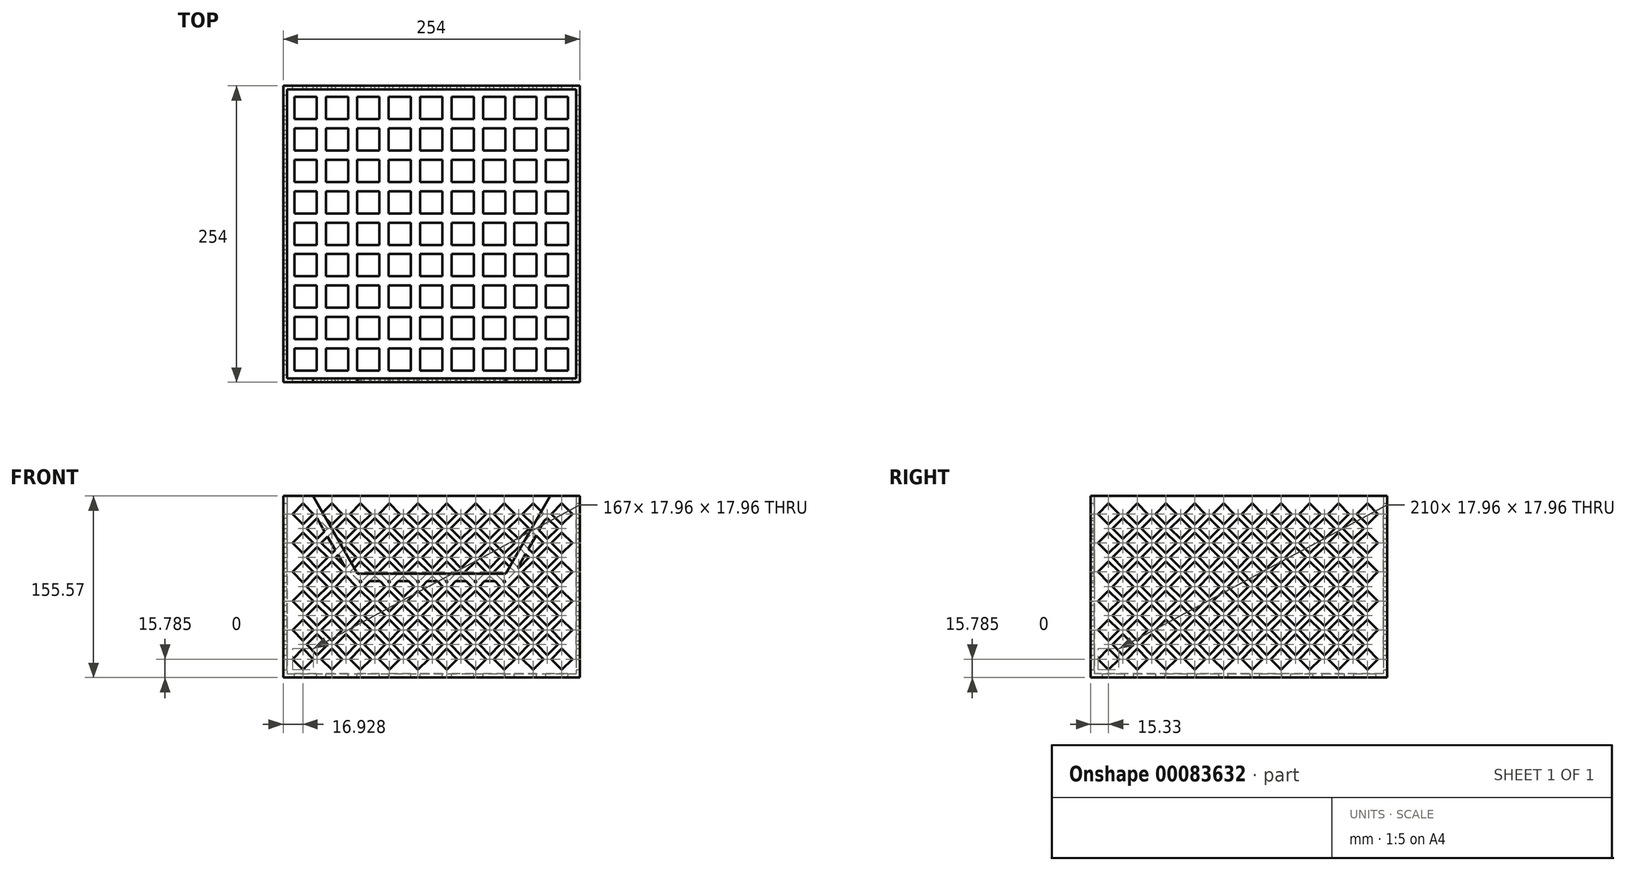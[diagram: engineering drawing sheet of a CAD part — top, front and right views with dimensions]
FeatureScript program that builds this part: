
annotation { "Feature Type Name" : "Feature", "Feature Type Description" : "" }
export const myFeature = defineFeature(function(context is Context, id is Id, definition is map)
    precondition{}
    {
        {
            var Q0;
            Q0=qCreatedBy(makeId("Top.planeOp"),FACE);
            var sketch = newSketch(context, id + "F0", { "sketchPlane" : qUnion([Q0])});
            skLineSegment(sketch, "E0.bottom", {"start": v(-127, 127) * mm, "end": v(127, 127) * mm});
            skLineSegment(sketch, "E0.top", {"start": v(-127, -127) * mm, "end": v(127, -127) * mm});
            skLineSegment(sketch, "E0.left", {"start": v(-127, 127) * mm, "end": v(-127, -127) * mm});
            skLineSegment(sketch, "E0.right", {"start": v(127, 127) * mm, "end": v(127, -127) * mm});
            skPoint(sketch, "E0.middle", {"position": v(0, 0) * mm});
            skSolve(sketch);
        }
        {
            var Q0;
            Q0 = qSketchRegion(id + "F0", true);
            extrude(context, id + "F1", {"entities" : qUnion([Q0]), "depth" : 3.17 * mm});
        }
        {
            var Q0;
            Q0=makeQuery(id+"F1.opExtrude","CAP_FACE",FACE,{"disambiguationData":[OSD([sQuery(id+"F0.wireOp",EDGE,"E0.bottom"),sQuery(id+"F0.wireOp",EDGE,"E0.top"),sQuery(id+"F0.wireOp",EDGE,"E0.left"),sQuery(id+"F0.wireOp",EDGE,"E0.right")])],"isStart":false});
            var sketch = newSketch(context, id + "F2", { "sketchPlane" : qUnion([Q0])});
            skLineSegment(sketch, "E1.bottom", {"start": v(-127, 127) * mm, "end": v(127, 127) * mm});
            skLineSegment(sketch, "E1.top", {"start": v(-127, -127) * mm, "end": v(127, -127) * mm});
            skLineSegment(sketch, "E1.left", {"start": v(-127, 127) * mm, "end": v(-127, -127) * mm});
            skLineSegment(sketch, "E1.right", {"start": v(127, 127) * mm, "end": v(127, -127) * mm});
            skPoint(sketch, "E1.middle", {"position": v(0, 0) * mm});
            skLineSegment(sketch, "E2.bottom", {"start": v(-123.82, 123.82) * mm, "end": v(123.82, 123.82) * mm});
            skLineSegment(sketch, "E2.top", {"start": v(-123.82, -123.82) * mm, "end": v(123.82, -123.82) * mm});
            skLineSegment(sketch, "E2.left", {"start": v(-123.82, 123.82) * mm, "end": v(-123.82, -123.82) * mm});
            skLineSegment(sketch, "E2.right", {"start": v(123.82, 123.82) * mm, "end": v(123.82, -123.82) * mm});
            skSolve(sketch);
        }
        {
            var Q0;
            Q0 = qSketchRegion(id + "F2", true);
            extrude(context, id + "F3", {"entities" : qUnion([Q0]), "operationType" : NewBodyOperationType.ADD, "depth" : 152.4 * mm});
        }
        {
            var Q0;
            Q0=makeQuery(id+"F3.boolean.opBoolean","MERGE",FACE,{"derivedFrom":[makeQuery(id+"F1.opExtrude","SWEPT_FACE",FACE,{"disambiguationData":[OSD([sQuery(id+"F0.wireOp",EDGE,"E0.top")])]}),makeQuery(id+"F3.opExtrude","SWEPT_FACE",FACE,{"disambiguationData":[OSD([sQuery(id+"F2.wireOp",EDGE,"E1.top")])]})]});
            var sketch = newSketch(context, id + "F4", { "sketchPlane" : qUnion([Q0])});
            skLineSegment(sketch, "E3", {"start": v(0, 155.58) * mm, "end": v(0, 88.9) * mm, "construction": true});
            skLineSegment(sketch, "E4", {"start": v(0, 88.9) * mm, "end": v(-63.5, 88.9) * mm});
            skLineSegment(sketch, "E5", {"start": v(-63.5, 88.9) * mm, "end": v(-101.6, 155.58) * mm});
            skLineSegment(sketch, "E6", {"start": v(-101.6, 155.58) * mm, "end": v(0, 155.58) * mm});
            skLineSegment(sketch, "E7.MirrorCS", {"start": v(0, 88.9) * mm, "end": v(63.5, 88.9) * mm});
            skLineSegment(sketch, "E8.MirrorCS", {"start": v(101.6, 155.58) * mm, "end": v(0, 155.58) * mm});
            skLineSegment(sketch, "E9.MirrorCS", {"start": v(63.5, 88.9) * mm, "end": v(101.6, 155.58) * mm});
            skSolve(sketch);
        }
        {
            var Q0;
            Q0 = qSketchRegion(id + "F4", true);
            extrude(context, id + "F5", {"entities" : qUnion([Q0]), "operationType" : NewBodyOperationType.REMOVE, "endBound" : BoundingType.UP_TO_NEXT, "oppositeDirection" : true, "depth" : 25.4 * mm});
        }
        {
            var Q0;
            Q0=makeQuery(id+"F3.boolean.opBoolean","MERGE",FACE,{"derivedFrom":[makeQuery(id+"F1.opExtrude","SWEPT_FACE",FACE,{"disambiguationData":[OSD([sQuery(id+"F0.wireOp",EDGE,"E0.right")])]}),makeQuery(id+"F3.opExtrude","SWEPT_FACE",FACE,{"disambiguationData":[OSD([sQuery(id+"F2.wireOp",EDGE,"E1.right")])]})]});
            var sketch = newSketch(context, id + "F6", { "sketchPlane" : qUnion([Q0])});
            skLineSegment(sketch, "E10", {"start": v(-111.67, 149.23) * mm, "end": v(-120.65, 140.24) * mm});
            skLineSegment(sketch, "E11", {"start": v(-120.65, 140.24) * mm, "end": v(-111.67, 131.26) * mm});
            skLineSegment(sketch, "E12", {"start": v(-111.67, 131.26) * mm, "end": v(-102.69, 140.24) * mm});
            skLineSegment(sketch, "E13", {"start": v(-102.69, 140.24) * mm, "end": v(-111.67, 149.23) * mm});
            skLineSegment(sketch, "E14", {"start": v(-111.67, 131.26) * mm, "end": v(-88.6, 131.26) * mm, "construction": true});
            skLineSegment(sketch, "E15.0.1.0", {"start": v(-120.65, 115.35) * mm, "end": v(-111.67, 106.37) * mm});
            skLineSegment(sketch, "E15.0.1.1", {"start": v(-111.67, 106.37) * mm, "end": v(-102.69, 115.35) * mm});
            skLineSegment(sketch, "E15.0.1.2", {"start": v(-102.69, 115.35) * mm, "end": v(-111.67, 124.33) * mm});
            skLineSegment(sketch, "E15.0.1.3", {"start": v(-111.67, 124.33) * mm, "end": v(-120.65, 115.35) * mm});
            skLineSegment(sketch, "E15.0.2.0", {"start": v(-120.65, 90.46) * mm, "end": v(-111.67, 81.48) * mm});
            skLineSegment(sketch, "E15.0.2.1", {"start": v(-111.67, 81.48) * mm, "end": v(-102.69, 90.46) * mm});
            skLineSegment(sketch, "E15.0.2.2", {"start": v(-102.69, 90.46) * mm, "end": v(-111.67, 99.44) * mm});
            skLineSegment(sketch, "E15.0.2.3", {"start": v(-111.67, 99.44) * mm, "end": v(-120.65, 90.46) * mm});
            skLineSegment(sketch, "E15.0.3.0", {"start": v(-120.65, 65.57) * mm, "end": v(-111.67, 56.59) * mm});
            skLineSegment(sketch, "E15.0.3.1", {"start": v(-111.67, 56.59) * mm, "end": v(-102.69, 65.57) * mm});
            skLineSegment(sketch, "E15.0.3.2", {"start": v(-102.69, 65.57) * mm, "end": v(-111.67, 74.55) * mm});
            skLineSegment(sketch, "E15.0.3.3", {"start": v(-111.67, 74.55) * mm, "end": v(-120.65, 65.57) * mm});
            skLineSegment(sketch, "E15.0.4.0", {"start": v(-120.65, 40.68) * mm, "end": v(-111.67, 31.7) * mm});
            skLineSegment(sketch, "E15.0.4.1", {"start": v(-111.67, 31.7) * mm, "end": v(-102.69, 40.68) * mm});
            skLineSegment(sketch, "E15.0.4.2", {"start": v(-102.69, 40.68) * mm, "end": v(-111.67, 49.66) * mm});
            skLineSegment(sketch, "E15.0.4.3", {"start": v(-111.67, 49.66) * mm, "end": v(-120.65, 40.68) * mm});
            skLineSegment(sketch, "E15.0.5.0", {"start": v(-120.65, 15.78) * mm, "end": v(-111.67, 6.8) * mm});
            skLineSegment(sketch, "E15.0.5.1", {"start": v(-111.67, 6.8) * mm, "end": v(-102.69, 15.78) * mm});
            skLineSegment(sketch, "E15.0.5.2", {"start": v(-102.69, 15.78) * mm, "end": v(-111.67, 24.77) * mm});
            skLineSegment(sketch, "E15.0.5.3", {"start": v(-111.67, 24.77) * mm, "end": v(-120.65, 15.78) * mm});
            skLineSegment(sketch, "E15.1.0.0", {"start": v(-96.01, 140.24) * mm, "end": v(-87.03, 131.26) * mm});
            skLineSegment(sketch, "E15.1.0.1", {"start": v(-87.03, 131.26) * mm, "end": v(-78.05, 140.24) * mm});
            skLineSegment(sketch, "E15.1.0.2", {"start": v(-78.05, 140.24) * mm, "end": v(-87.03, 149.23) * mm});
            skLineSegment(sketch, "E15.1.0.3", {"start": v(-87.03, 149.23) * mm, "end": v(-96.01, 140.24) * mm});
            skLineSegment(sketch, "E15.1.1.0", {"start": v(-96.01, 115.35) * mm, "end": v(-87.03, 106.37) * mm});
            skLineSegment(sketch, "E15.1.1.1", {"start": v(-87.03, 106.37) * mm, "end": v(-78.05, 115.35) * mm});
            skLineSegment(sketch, "E15.1.1.2", {"start": v(-78.05, 115.35) * mm, "end": v(-87.03, 124.33) * mm});
            skLineSegment(sketch, "E15.1.1.3", {"start": v(-87.03, 124.33) * mm, "end": v(-96.01, 115.35) * mm});
            skLineSegment(sketch, "E15.1.2.0", {"start": v(-96.01, 90.46) * mm, "end": v(-87.03, 81.48) * mm});
            skLineSegment(sketch, "E15.1.2.1", {"start": v(-87.03, 81.48) * mm, "end": v(-78.05, 90.46) * mm});
            skLineSegment(sketch, "E15.1.2.2", {"start": v(-78.05, 90.46) * mm, "end": v(-87.03, 99.44) * mm});
            skLineSegment(sketch, "E15.1.2.3", {"start": v(-87.03, 99.44) * mm, "end": v(-96.01, 90.46) * mm});
            skLineSegment(sketch, "E15.1.3.0", {"start": v(-96.01, 65.57) * mm, "end": v(-87.03, 56.59) * mm});
            skLineSegment(sketch, "E15.1.3.1", {"start": v(-87.03, 56.59) * mm, "end": v(-78.05, 65.57) * mm});
            skLineSegment(sketch, "E15.1.3.2", {"start": v(-78.05, 65.57) * mm, "end": v(-87.03, 74.55) * mm});
            skLineSegment(sketch, "E15.1.3.3", {"start": v(-87.03, 74.55) * mm, "end": v(-96.01, 65.57) * mm});
            skLineSegment(sketch, "E15.1.4.0", {"start": v(-96.01, 40.68) * mm, "end": v(-87.03, 31.7) * mm});
            skLineSegment(sketch, "E15.1.4.1", {"start": v(-87.03, 31.7) * mm, "end": v(-78.05, 40.68) * mm});
            skLineSegment(sketch, "E15.1.4.2", {"start": v(-78.05, 40.68) * mm, "end": v(-87.03, 49.66) * mm});
            skLineSegment(sketch, "E15.1.4.3", {"start": v(-87.03, 49.66) * mm, "end": v(-96.01, 40.68) * mm});
            skLineSegment(sketch, "E15.1.5.0", {"start": v(-96.01, 15.78) * mm, "end": v(-87.03, 6.8) * mm});
            skLineSegment(sketch, "E15.1.5.1", {"start": v(-87.03, 6.8) * mm, "end": v(-78.05, 15.78) * mm});
            skLineSegment(sketch, "E15.1.5.2", {"start": v(-78.05, 15.78) * mm, "end": v(-87.03, 24.77) * mm});
            skLineSegment(sketch, "E15.1.5.3", {"start": v(-87.03, 24.77) * mm, "end": v(-96.01, 15.78) * mm});
            skLineSegment(sketch, "E15.2.0.0", {"start": v(-71.37, 140.24) * mm, "end": v(-62.4, 131.26) * mm});
            skLineSegment(sketch, "E15.2.0.1", {"start": v(-62.4, 131.26) * mm, "end": v(-53.41, 140.24) * mm});
            skLineSegment(sketch, "E15.2.0.2", {"start": v(-53.41, 140.24) * mm, "end": v(-62.4, 149.23) * mm});
            skLineSegment(sketch, "E15.2.0.3", {"start": v(-62.4, 149.23) * mm, "end": v(-71.37, 140.24) * mm});
            skLineSegment(sketch, "E15.2.1.0", {"start": v(-71.37, 115.35) * mm, "end": v(-62.4, 106.37) * mm});
            skLineSegment(sketch, "E15.2.1.1", {"start": v(-62.4, 106.37) * mm, "end": v(-53.41, 115.35) * mm});
            skLineSegment(sketch, "E15.2.1.2", {"start": v(-53.41, 115.35) * mm, "end": v(-62.4, 124.33) * mm});
            skLineSegment(sketch, "E15.2.1.3", {"start": v(-62.4, 124.33) * mm, "end": v(-71.37, 115.35) * mm});
            skLineSegment(sketch, "E15.2.2.0", {"start": v(-71.37, 90.46) * mm, "end": v(-62.4, 81.48) * mm});
            skLineSegment(sketch, "E15.2.2.1", {"start": v(-62.4, 81.48) * mm, "end": v(-53.41, 90.46) * mm});
            skLineSegment(sketch, "E15.2.2.2", {"start": v(-53.41, 90.46) * mm, "end": v(-62.4, 99.44) * mm});
            skLineSegment(sketch, "E15.2.2.3", {"start": v(-62.4, 99.44) * mm, "end": v(-71.37, 90.46) * mm});
            skLineSegment(sketch, "E15.2.3.0", {"start": v(-71.37, 65.57) * mm, "end": v(-62.4, 56.59) * mm});
            skLineSegment(sketch, "E15.2.3.1", {"start": v(-62.4, 56.59) * mm, "end": v(-53.41, 65.57) * mm});
            skLineSegment(sketch, "E15.2.3.2", {"start": v(-53.41, 65.57) * mm, "end": v(-62.4, 74.55) * mm});
            skLineSegment(sketch, "E15.2.3.3", {"start": v(-62.4, 74.55) * mm, "end": v(-71.37, 65.57) * mm});
            skLineSegment(sketch, "E15.2.4.0", {"start": v(-71.37, 40.68) * mm, "end": v(-62.4, 31.7) * mm});
            skLineSegment(sketch, "E15.2.4.1", {"start": v(-62.4, 31.7) * mm, "end": v(-53.41, 40.68) * mm});
            skLineSegment(sketch, "E15.2.4.2", {"start": v(-53.41, 40.68) * mm, "end": v(-62.4, 49.66) * mm});
            skLineSegment(sketch, "E15.2.4.3", {"start": v(-62.4, 49.66) * mm, "end": v(-71.37, 40.68) * mm});
            skLineSegment(sketch, "E15.2.5.0", {"start": v(-71.37, 15.78) * mm, "end": v(-62.4, 6.8) * mm});
            skLineSegment(sketch, "E15.2.5.1", {"start": v(-62.4, 6.8) * mm, "end": v(-53.41, 15.78) * mm});
            skLineSegment(sketch, "E15.2.5.2", {"start": v(-53.41, 15.78) * mm, "end": v(-62.4, 24.77) * mm});
            skLineSegment(sketch, "E15.2.5.3", {"start": v(-62.4, 24.77) * mm, "end": v(-71.37, 15.78) * mm});
            skLineSegment(sketch, "E15.3.0.0", {"start": v(-46.74, 140.24) * mm, "end": v(-37.76, 131.26) * mm});
            skLineSegment(sketch, "E15.3.0.1", {"start": v(-37.76, 131.26) * mm, "end": v(-28.78, 140.24) * mm});
            skLineSegment(sketch, "E15.3.0.2", {"start": v(-28.78, 140.24) * mm, "end": v(-37.76, 149.23) * mm});
            skLineSegment(sketch, "E15.3.0.3", {"start": v(-37.76, 149.23) * mm, "end": v(-46.74, 140.24) * mm});
            skLineSegment(sketch, "E15.3.1.0", {"start": v(-46.74, 115.35) * mm, "end": v(-37.76, 106.37) * mm});
            skLineSegment(sketch, "E15.3.1.1", {"start": v(-37.76, 106.37) * mm, "end": v(-28.78, 115.35) * mm});
            skLineSegment(sketch, "E15.3.1.2", {"start": v(-28.78, 115.35) * mm, "end": v(-37.76, 124.33) * mm});
            skLineSegment(sketch, "E15.3.1.3", {"start": v(-37.76, 124.33) * mm, "end": v(-46.74, 115.35) * mm});
            skLineSegment(sketch, "E15.3.2.0", {"start": v(-46.74, 90.46) * mm, "end": v(-37.76, 81.48) * mm});
            skLineSegment(sketch, "E15.3.2.1", {"start": v(-37.76, 81.48) * mm, "end": v(-28.78, 90.46) * mm});
            skLineSegment(sketch, "E15.3.2.2", {"start": v(-28.78, 90.46) * mm, "end": v(-37.76, 99.44) * mm});
            skLineSegment(sketch, "E15.3.2.3", {"start": v(-37.76, 99.44) * mm, "end": v(-46.74, 90.46) * mm});
            skLineSegment(sketch, "E15.3.3.0", {"start": v(-46.74, 65.57) * mm, "end": v(-37.76, 56.59) * mm});
            skLineSegment(sketch, "E15.3.3.1", {"start": v(-37.76, 56.59) * mm, "end": v(-28.78, 65.57) * mm});
            skLineSegment(sketch, "E15.3.3.2", {"start": v(-28.78, 65.57) * mm, "end": v(-37.76, 74.55) * mm});
            skLineSegment(sketch, "E15.3.3.3", {"start": v(-37.76, 74.55) * mm, "end": v(-46.74, 65.57) * mm});
            skLineSegment(sketch, "E15.3.4.0", {"start": v(-46.74, 40.68) * mm, "end": v(-37.76, 31.7) * mm});
            skLineSegment(sketch, "E15.3.4.1", {"start": v(-37.76, 31.7) * mm, "end": v(-28.78, 40.68) * mm});
            skLineSegment(sketch, "E15.3.4.2", {"start": v(-28.78, 40.68) * mm, "end": v(-37.76, 49.66) * mm});
            skLineSegment(sketch, "E15.3.4.3", {"start": v(-37.76, 49.66) * mm, "end": v(-46.74, 40.68) * mm});
            skLineSegment(sketch, "E15.3.5.0", {"start": v(-46.74, 15.78) * mm, "end": v(-37.76, 6.8) * mm});
            skLineSegment(sketch, "E15.3.5.1", {"start": v(-37.76, 6.8) * mm, "end": v(-28.78, 15.78) * mm});
            skLineSegment(sketch, "E15.3.5.2", {"start": v(-28.78, 15.78) * mm, "end": v(-37.76, 24.77) * mm});
            skLineSegment(sketch, "E15.3.5.3", {"start": v(-37.76, 24.77) * mm, "end": v(-46.74, 15.78) * mm});
            skLineSegment(sketch, "E15.4.0.0", {"start": v(-22.1, 140.24) * mm, "end": v(-13.12, 131.26) * mm});
            skLineSegment(sketch, "E15.4.0.1", {"start": v(-13.12, 131.26) * mm, "end": v(-4.14, 140.24) * mm});
            skLineSegment(sketch, "E15.4.0.2", {"start": v(-4.14, 140.24) * mm, "end": v(-13.12, 149.23) * mm});
            skLineSegment(sketch, "E15.4.0.3", {"start": v(-13.12, 149.23) * mm, "end": v(-22.1, 140.24) * mm});
            skLineSegment(sketch, "E15.4.1.0", {"start": v(-22.1, 115.35) * mm, "end": v(-13.12, 106.37) * mm});
            skLineSegment(sketch, "E15.4.1.1", {"start": v(-13.12, 106.37) * mm, "end": v(-4.14, 115.35) * mm});
            skLineSegment(sketch, "E15.4.1.2", {"start": v(-4.14, 115.35) * mm, "end": v(-13.12, 124.33) * mm});
            skLineSegment(sketch, "E15.4.1.3", {"start": v(-13.12, 124.33) * mm, "end": v(-22.1, 115.35) * mm});
            skLineSegment(sketch, "E15.4.2.0", {"start": v(-22.1, 90.46) * mm, "end": v(-13.12, 81.48) * mm});
            skLineSegment(sketch, "E15.4.2.1", {"start": v(-13.12, 81.48) * mm, "end": v(-4.14, 90.46) * mm});
            skLineSegment(sketch, "E15.4.2.2", {"start": v(-4.14, 90.46) * mm, "end": v(-13.12, 99.44) * mm});
            skLineSegment(sketch, "E15.4.2.3", {"start": v(-13.12, 99.44) * mm, "end": v(-22.1, 90.46) * mm});
            skLineSegment(sketch, "E15.4.3.0", {"start": v(-22.1, 65.57) * mm, "end": v(-13.12, 56.59) * mm});
            skLineSegment(sketch, "E15.4.3.1", {"start": v(-13.12, 56.59) * mm, "end": v(-4.14, 65.57) * mm});
            skLineSegment(sketch, "E15.4.3.2", {"start": v(-4.14, 65.57) * mm, "end": v(-13.12, 74.55) * mm});
            skLineSegment(sketch, "E15.4.3.3", {"start": v(-13.12, 74.55) * mm, "end": v(-22.1, 65.57) * mm});
            skLineSegment(sketch, "E15.4.4.0", {"start": v(-22.1, 40.68) * mm, "end": v(-13.12, 31.7) * mm});
            skLineSegment(sketch, "E15.4.4.1", {"start": v(-13.12, 31.7) * mm, "end": v(-4.14, 40.68) * mm});
            skLineSegment(sketch, "E15.4.4.2", {"start": v(-4.14, 40.68) * mm, "end": v(-13.12, 49.66) * mm});
            skLineSegment(sketch, "E15.4.4.3", {"start": v(-13.12, 49.66) * mm, "end": v(-22.1, 40.68) * mm});
            skLineSegment(sketch, "E15.4.5.0", {"start": v(-22.1, 15.78) * mm, "end": v(-13.12, 6.8) * mm});
            skLineSegment(sketch, "E15.4.5.1", {"start": v(-13.12, 6.8) * mm, "end": v(-4.14, 15.78) * mm});
            skLineSegment(sketch, "E15.4.5.2", {"start": v(-4.14, 15.78) * mm, "end": v(-13.12, 24.77) * mm});
            skLineSegment(sketch, "E15.4.5.3", {"start": v(-13.12, 24.77) * mm, "end": v(-22.1, 15.78) * mm});
            skLineSegment(sketch, "E15.5.0.0", {"start": v(2.54, 140.24) * mm, "end": v(11.52, 131.26) * mm});
            skLineSegment(sketch, "E15.5.0.1", {"start": v(11.52, 131.26) * mm, "end": v(20.5, 140.24) * mm});
            skLineSegment(sketch, "E15.5.0.2", {"start": v(20.5, 140.24) * mm, "end": v(11.52, 149.23) * mm});
            skLineSegment(sketch, "E15.5.0.3", {"start": v(11.52, 149.23) * mm, "end": v(2.54, 140.24) * mm});
            skLineSegment(sketch, "E15.5.1.0", {"start": v(2.54, 115.35) * mm, "end": v(11.52, 106.37) * mm});
            skLineSegment(sketch, "E15.5.1.1", {"start": v(11.52, 106.37) * mm, "end": v(20.5, 115.35) * mm});
            skLineSegment(sketch, "E15.5.1.2", {"start": v(20.5, 115.35) * mm, "end": v(11.52, 124.33) * mm});
            skLineSegment(sketch, "E15.5.1.3", {"start": v(11.52, 124.33) * mm, "end": v(2.54, 115.35) * mm});
            skLineSegment(sketch, "E15.5.2.0", {"start": v(2.54, 90.46) * mm, "end": v(11.52, 81.48) * mm});
            skLineSegment(sketch, "E15.5.2.1", {"start": v(11.52, 81.48) * mm, "end": v(20.5, 90.46) * mm});
            skLineSegment(sketch, "E15.5.2.2", {"start": v(20.5, 90.46) * mm, "end": v(11.52, 99.44) * mm});
            skLineSegment(sketch, "E15.5.2.3", {"start": v(11.52, 99.44) * mm, "end": v(2.54, 90.46) * mm});
            skLineSegment(sketch, "E15.5.3.0", {"start": v(2.54, 65.57) * mm, "end": v(11.52, 56.59) * mm});
            skLineSegment(sketch, "E15.5.3.1", {"start": v(11.52, 56.59) * mm, "end": v(20.5, 65.57) * mm});
            skLineSegment(sketch, "E15.5.3.2", {"start": v(20.5, 65.57) * mm, "end": v(11.52, 74.55) * mm});
            skLineSegment(sketch, "E15.5.3.3", {"start": v(11.52, 74.55) * mm, "end": v(2.54, 65.57) * mm});
            skLineSegment(sketch, "E15.5.4.0", {"start": v(2.54, 40.68) * mm, "end": v(11.52, 31.7) * mm});
            skLineSegment(sketch, "E15.5.4.1", {"start": v(11.52, 31.7) * mm, "end": v(20.5, 40.68) * mm});
            skLineSegment(sketch, "E15.5.4.2", {"start": v(20.5, 40.68) * mm, "end": v(11.52, 49.66) * mm});
            skLineSegment(sketch, "E15.5.4.3", {"start": v(11.52, 49.66) * mm, "end": v(2.54, 40.68) * mm});
            skLineSegment(sketch, "E15.5.5.0", {"start": v(2.54, 15.78) * mm, "end": v(11.52, 6.8) * mm});
            skLineSegment(sketch, "E15.5.5.1", {"start": v(11.52, 6.8) * mm, "end": v(20.5, 15.78) * mm});
            skLineSegment(sketch, "E15.5.5.2", {"start": v(20.5, 15.78) * mm, "end": v(11.52, 24.77) * mm});
            skLineSegment(sketch, "E15.5.5.3", {"start": v(11.52, 24.77) * mm, "end": v(2.54, 15.78) * mm});
            skLineSegment(sketch, "E15.6.0.0", {"start": v(27.18, 140.24) * mm, "end": v(36.16, 131.26) * mm});
            skLineSegment(sketch, "E15.6.0.1", {"start": v(36.16, 131.26) * mm, "end": v(45.14, 140.24) * mm});
            skLineSegment(sketch, "E15.6.0.2", {"start": v(45.14, 140.24) * mm, "end": v(36.16, 149.23) * mm});
            skLineSegment(sketch, "E15.6.0.3", {"start": v(36.16, 149.23) * mm, "end": v(27.18, 140.24) * mm});
            skLineSegment(sketch, "E15.6.1.0", {"start": v(27.18, 115.35) * mm, "end": v(36.16, 106.37) * mm});
            skLineSegment(sketch, "E15.6.1.1", {"start": v(36.16, 106.37) * mm, "end": v(45.14, 115.35) * mm});
            skLineSegment(sketch, "E15.6.1.2", {"start": v(45.14, 115.35) * mm, "end": v(36.16, 124.33) * mm});
            skLineSegment(sketch, "E15.6.1.3", {"start": v(36.16, 124.33) * mm, "end": v(27.18, 115.35) * mm});
            skLineSegment(sketch, "E15.6.2.0", {"start": v(27.18, 90.46) * mm, "end": v(36.16, 81.48) * mm});
            skLineSegment(sketch, "E15.6.2.1", {"start": v(36.16, 81.48) * mm, "end": v(45.14, 90.46) * mm});
            skLineSegment(sketch, "E15.6.2.2", {"start": v(45.14, 90.46) * mm, "end": v(36.16, 99.44) * mm});
            skLineSegment(sketch, "E15.6.2.3", {"start": v(36.16, 99.44) * mm, "end": v(27.18, 90.46) * mm});
            skLineSegment(sketch, "E15.6.3.0", {"start": v(27.18, 65.57) * mm, "end": v(36.16, 56.59) * mm});
            skLineSegment(sketch, "E15.6.3.1", {"start": v(36.16, 56.59) * mm, "end": v(45.14, 65.57) * mm});
            skLineSegment(sketch, "E15.6.3.2", {"start": v(45.14, 65.57) * mm, "end": v(36.16, 74.55) * mm});
            skLineSegment(sketch, "E15.6.3.3", {"start": v(36.16, 74.55) * mm, "end": v(27.18, 65.57) * mm});
            skLineSegment(sketch, "E15.6.4.0", {"start": v(27.18, 40.68) * mm, "end": v(36.16, 31.7) * mm});
            skLineSegment(sketch, "E15.6.4.1", {"start": v(36.16, 31.7) * mm, "end": v(45.14, 40.68) * mm});
            skLineSegment(sketch, "E15.6.4.2", {"start": v(45.14, 40.68) * mm, "end": v(36.16, 49.66) * mm});
            skLineSegment(sketch, "E15.6.4.3", {"start": v(36.16, 49.66) * mm, "end": v(27.18, 40.68) * mm});
            skLineSegment(sketch, "E15.6.5.0", {"start": v(27.18, 15.78) * mm, "end": v(36.16, 6.8) * mm});
            skLineSegment(sketch, "E15.6.5.1", {"start": v(36.16, 6.8) * mm, "end": v(45.14, 15.78) * mm});
            skLineSegment(sketch, "E15.6.5.2", {"start": v(45.14, 15.78) * mm, "end": v(36.16, 24.77) * mm});
            skLineSegment(sketch, "E15.6.5.3", {"start": v(36.16, 24.77) * mm, "end": v(27.18, 15.78) * mm});
            skLineSegment(sketch, "E15.7.0.0", {"start": v(51.82, 140.24) * mm, "end": v(60.8, 131.26) * mm});
            skLineSegment(sketch, "E15.7.0.1", {"start": v(60.8, 131.26) * mm, "end": v(69.78, 140.24) * mm});
            skLineSegment(sketch, "E15.7.0.2", {"start": v(69.78, 140.24) * mm, "end": v(60.8, 149.23) * mm});
            skLineSegment(sketch, "E15.7.0.3", {"start": v(60.8, 149.23) * mm, "end": v(51.82, 140.24) * mm});
            skLineSegment(sketch, "E15.7.1.0", {"start": v(51.82, 115.35) * mm, "end": v(60.8, 106.37) * mm});
            skLineSegment(sketch, "E15.7.1.1", {"start": v(60.8, 106.37) * mm, "end": v(69.78, 115.35) * mm});
            skLineSegment(sketch, "E15.7.1.2", {"start": v(69.78, 115.35) * mm, "end": v(60.8, 124.33) * mm});
            skLineSegment(sketch, "E15.7.1.3", {"start": v(60.8, 124.33) * mm, "end": v(51.82, 115.35) * mm});
            skLineSegment(sketch, "E15.7.2.0", {"start": v(51.82, 90.46) * mm, "end": v(60.8, 81.48) * mm});
            skLineSegment(sketch, "E15.7.2.1", {"start": v(60.8, 81.48) * mm, "end": v(69.78, 90.46) * mm});
            skLineSegment(sketch, "E15.7.2.2", {"start": v(69.78, 90.46) * mm, "end": v(60.8, 99.44) * mm});
            skLineSegment(sketch, "E15.7.2.3", {"start": v(60.8, 99.44) * mm, "end": v(51.82, 90.46) * mm});
            skLineSegment(sketch, "E15.7.3.0", {"start": v(51.82, 65.57) * mm, "end": v(60.8, 56.59) * mm});
            skLineSegment(sketch, "E15.7.3.1", {"start": v(60.8, 56.59) * mm, "end": v(69.78, 65.57) * mm});
            skLineSegment(sketch, "E15.7.3.2", {"start": v(69.78, 65.57) * mm, "end": v(60.8, 74.55) * mm});
            skLineSegment(sketch, "E15.7.3.3", {"start": v(60.8, 74.55) * mm, "end": v(51.82, 65.57) * mm});
            skLineSegment(sketch, "E15.7.4.0", {"start": v(51.82, 40.68) * mm, "end": v(60.8, 31.7) * mm});
            skLineSegment(sketch, "E15.7.4.1", {"start": v(60.8, 31.7) * mm, "end": v(69.78, 40.68) * mm});
            skLineSegment(sketch, "E15.7.4.2", {"start": v(69.78, 40.68) * mm, "end": v(60.8, 49.66) * mm});
            skLineSegment(sketch, "E15.7.4.3", {"start": v(60.8, 49.66) * mm, "end": v(51.82, 40.68) * mm});
            skLineSegment(sketch, "E15.7.5.0", {"start": v(51.82, 15.78) * mm, "end": v(60.8, 6.8) * mm});
            skLineSegment(sketch, "E15.7.5.1", {"start": v(60.8, 6.8) * mm, "end": v(69.78, 15.78) * mm});
            skLineSegment(sketch, "E15.7.5.2", {"start": v(69.78, 15.78) * mm, "end": v(60.8, 24.77) * mm});
            skLineSegment(sketch, "E15.7.5.3", {"start": v(60.8, 24.77) * mm, "end": v(51.82, 15.78) * mm});
            skLineSegment(sketch, "E15.8.0.0", {"start": v(76.45, 140.24) * mm, "end": v(85.43, 131.26) * mm});
            skLineSegment(sketch, "E15.8.0.1", {"start": v(85.43, 131.26) * mm, "end": v(94.41, 140.24) * mm});
            skLineSegment(sketch, "E15.8.0.2", {"start": v(94.41, 140.24) * mm, "end": v(85.43, 149.23) * mm});
            skLineSegment(sketch, "E15.8.0.3", {"start": v(85.43, 149.23) * mm, "end": v(76.45, 140.24) * mm});
            skLineSegment(sketch, "E15.8.1.0", {"start": v(76.45, 115.35) * mm, "end": v(85.43, 106.37) * mm});
            skLineSegment(sketch, "E15.8.1.1", {"start": v(85.43, 106.37) * mm, "end": v(94.41, 115.35) * mm});
            skLineSegment(sketch, "E15.8.1.2", {"start": v(94.41, 115.35) * mm, "end": v(85.43, 124.33) * mm});
            skLineSegment(sketch, "E15.8.1.3", {"start": v(85.43, 124.33) * mm, "end": v(76.45, 115.35) * mm});
            skLineSegment(sketch, "E15.8.2.0", {"start": v(76.45, 90.46) * mm, "end": v(85.43, 81.48) * mm});
            skLineSegment(sketch, "E15.8.2.1", {"start": v(85.43, 81.48) * mm, "end": v(94.41, 90.46) * mm});
            skLineSegment(sketch, "E15.8.2.2", {"start": v(94.41, 90.46) * mm, "end": v(85.43, 99.44) * mm});
            skLineSegment(sketch, "E15.8.2.3", {"start": v(85.43, 99.44) * mm, "end": v(76.45, 90.46) * mm});
            skLineSegment(sketch, "E15.8.3.0", {"start": v(76.45, 65.57) * mm, "end": v(85.43, 56.59) * mm});
            skLineSegment(sketch, "E15.8.3.1", {"start": v(85.43, 56.59) * mm, "end": v(94.41, 65.57) * mm});
            skLineSegment(sketch, "E15.8.3.2", {"start": v(94.41, 65.57) * mm, "end": v(85.43, 74.55) * mm});
            skLineSegment(sketch, "E15.8.3.3", {"start": v(85.43, 74.55) * mm, "end": v(76.45, 65.57) * mm});
            skLineSegment(sketch, "E15.8.4.0", {"start": v(76.45, 40.68) * mm, "end": v(85.43, 31.7) * mm});
            skLineSegment(sketch, "E15.8.4.1", {"start": v(85.43, 31.7) * mm, "end": v(94.41, 40.68) * mm});
            skLineSegment(sketch, "E15.8.4.2", {"start": v(94.41, 40.68) * mm, "end": v(85.43, 49.66) * mm});
            skLineSegment(sketch, "E15.8.4.3", {"start": v(85.43, 49.66) * mm, "end": v(76.45, 40.68) * mm});
            skLineSegment(sketch, "E15.8.5.0", {"start": v(76.45, 15.78) * mm, "end": v(85.43, 6.8) * mm});
            skLineSegment(sketch, "E15.8.5.1", {"start": v(85.43, 6.8) * mm, "end": v(94.41, 15.78) * mm});
            skLineSegment(sketch, "E15.8.5.2", {"start": v(94.41, 15.78) * mm, "end": v(85.43, 24.77) * mm});
            skLineSegment(sketch, "E15.8.5.3", {"start": v(85.43, 24.77) * mm, "end": v(76.45, 15.78) * mm});
            skLineSegment(sketch, "E15.9.0.0", {"start": v(101.1, 140.24) * mm, "end": v(110.07, 131.26) * mm});
            skLineSegment(sketch, "E15.9.0.1", {"start": v(110.07, 131.26) * mm, "end": v(119.05, 140.24) * mm});
            skLineSegment(sketch, "E15.9.0.2", {"start": v(119.05, 140.24) * mm, "end": v(110.07, 149.23) * mm});
            skLineSegment(sketch, "E15.9.0.3", {"start": v(110.07, 149.23) * mm, "end": v(101.1, 140.24) * mm});
            skLineSegment(sketch, "E15.9.1.0", {"start": v(101.1, 115.35) * mm, "end": v(110.07, 106.37) * mm});
            skLineSegment(sketch, "E15.9.1.1", {"start": v(110.07, 106.37) * mm, "end": v(119.05, 115.35) * mm});
            skLineSegment(sketch, "E15.9.1.2", {"start": v(119.05, 115.35) * mm, "end": v(110.07, 124.33) * mm});
            skLineSegment(sketch, "E15.9.1.3", {"start": v(110.07, 124.33) * mm, "end": v(101.1, 115.35) * mm});
            skLineSegment(sketch, "E15.9.2.0", {"start": v(101.1, 90.46) * mm, "end": v(110.07, 81.48) * mm});
            skLineSegment(sketch, "E15.9.2.1", {"start": v(110.07, 81.48) * mm, "end": v(119.05, 90.46) * mm});
            skLineSegment(sketch, "E15.9.2.2", {"start": v(119.05, 90.46) * mm, "end": v(110.07, 99.44) * mm});
            skLineSegment(sketch, "E15.9.2.3", {"start": v(110.07, 99.44) * mm, "end": v(101.1, 90.46) * mm});
            skLineSegment(sketch, "E15.9.3.0", {"start": v(101.1, 65.57) * mm, "end": v(110.07, 56.59) * mm});
            skLineSegment(sketch, "E15.9.3.1", {"start": v(110.07, 56.59) * mm, "end": v(119.05, 65.57) * mm});
            skLineSegment(sketch, "E15.9.3.2", {"start": v(119.05, 65.57) * mm, "end": v(110.07, 74.55) * mm});
            skLineSegment(sketch, "E15.9.3.3", {"start": v(110.07, 74.55) * mm, "end": v(101.1, 65.57) * mm});
            skLineSegment(sketch, "E15.9.4.0", {"start": v(101.1, 40.68) * mm, "end": v(110.07, 31.7) * mm});
            skLineSegment(sketch, "E15.9.4.1", {"start": v(110.07, 31.7) * mm, "end": v(119.05, 40.68) * mm});
            skLineSegment(sketch, "E15.9.4.2", {"start": v(119.05, 40.68) * mm, "end": v(110.07, 49.66) * mm});
            skLineSegment(sketch, "E15.9.4.3", {"start": v(110.07, 49.66) * mm, "end": v(101.1, 40.68) * mm});
            skLineSegment(sketch, "E15.9.5.0", {"start": v(101.1, 15.78) * mm, "end": v(110.07, 6.8) * mm});
            skLineSegment(sketch, "E15.9.5.1", {"start": v(110.07, 6.8) * mm, "end": v(119.05, 15.78) * mm});
            skLineSegment(sketch, "E15.9.5.2", {"start": v(119.05, 15.78) * mm, "end": v(110.07, 24.77) * mm});
            skLineSegment(sketch, "E15.9.5.3", {"start": v(110.07, 24.77) * mm, "end": v(101.1, 15.78) * mm});
            skLineSegment(sketch, "E15.direction1", {"start": v(-111.67, 131.26) * mm, "end": v(-87.03, 131.26) * mm, "construction": true});
            skLineSegment(sketch, "E15.direction2", {"start": v(-111.67, 131.26) * mm, "end": v(-111.67, 106.37) * mm, "construction": true});
            skSolve(sketch);
        }
        {
            var Q0;
            Q0 = qSketchRegion(id + "F6", true);
            extrude(context, id + "F7", {"entities" : qUnion([Q0]), "operationType" : NewBodyOperationType.REMOVE, "endBound" : BoundingType.THROUGH_ALL, "oppositeDirection" : true, "depth" : 25.4 * mm});
        }
        {
            var Q0;
            Q0=makeQuery(id+"F3.boolean.opBoolean","MERGE",FACE,{"derivedFrom":[makeQuery(id+"F1.opExtrude","SWEPT_FACE",FACE,{"disambiguationData":[OSD([sQuery(id+"F0.wireOp",EDGE,"E0.right")])]}),makeQuery(id+"F3.opExtrude","SWEPT_FACE",FACE,{"disambiguationData":[OSD([sQuery(id+"F2.wireOp",EDGE,"E1.right")])]})]});
            var sketch = newSketch(context, id + "F8", { "sketchPlane" : qUnion([Q0])});
            skLineSegment(sketch, "E16", {"start": v(-99.22, 136.78) * mm, "end": v(-108.2, 127.8) * mm});
            skLineSegment(sketch, "E17", {"start": v(-108.2, 127.8) * mm, "end": v(-99.22, 118.82) * mm});
            skLineSegment(sketch, "E18", {"start": v(-99.22, 118.82) * mm, "end": v(-90.24, 127.8) * mm});
            skLineSegment(sketch, "E19", {"start": v(-90.24, 127.8) * mm, "end": v(-99.22, 136.78) * mm});
            skLineSegment(sketch, "E20.0.1.0", {"start": v(-90.24, 102.9) * mm, "end": v(-99.22, 111.89) * mm});
            skLineSegment(sketch, "E20.0.1.1", {"start": v(-99.22, 93.93) * mm, "end": v(-90.24, 102.9) * mm});
            skLineSegment(sketch, "E20.0.1.2", {"start": v(-108.2, 102.9) * mm, "end": v(-99.22, 93.93) * mm});
            skLineSegment(sketch, "E20.0.1.3", {"start": v(-99.22, 111.89) * mm, "end": v(-108.2, 102.9) * mm});
            skLineSegment(sketch, "E20.0.2.0", {"start": v(-90.24, 78.01) * mm, "end": v(-99.22, 87) * mm});
            skLineSegment(sketch, "E20.0.2.1", {"start": v(-99.22, 69.03) * mm, "end": v(-90.24, 78.01) * mm});
            skLineSegment(sketch, "E20.0.2.2", {"start": v(-108.2, 78.01) * mm, "end": v(-99.22, 69.03) * mm});
            skLineSegment(sketch, "E20.0.2.3", {"start": v(-99.22, 87) * mm, "end": v(-108.2, 78.01) * mm});
            skLineSegment(sketch, "E20.0.3.0", {"start": v(-90.24, 53.12) * mm, "end": v(-99.22, 62.1) * mm});
            skLineSegment(sketch, "E20.0.3.1", {"start": v(-99.22, 44.14) * mm, "end": v(-90.24, 53.12) * mm});
            skLineSegment(sketch, "E20.0.3.2", {"start": v(-108.2, 53.12) * mm, "end": v(-99.22, 44.14) * mm});
            skLineSegment(sketch, "E20.0.3.3", {"start": v(-99.22, 62.1) * mm, "end": v(-108.2, 53.12) * mm});
            skLineSegment(sketch, "E20.0.4.0", {"start": v(-90.24, 28.23) * mm, "end": v(-99.22, 37.21) * mm});
            skLineSegment(sketch, "E20.0.4.1", {"start": v(-99.22, 19.25) * mm, "end": v(-90.24, 28.23) * mm});
            skLineSegment(sketch, "E20.0.4.2", {"start": v(-108.2, 28.23) * mm, "end": v(-99.22, 19.25) * mm});
            skLineSegment(sketch, "E20.0.4.3", {"start": v(-99.22, 37.21) * mm, "end": v(-108.2, 28.23) * mm});
            skLineSegment(sketch, "E20.1.0.0", {"start": v(-65.6, 127.8) * mm, "end": v(-74.59, 136.78) * mm});
            skLineSegment(sketch, "E20.1.0.1", {"start": v(-74.59, 118.82) * mm, "end": v(-65.6, 127.8) * mm});
            skLineSegment(sketch, "E20.1.0.2", {"start": v(-83.57, 127.8) * mm, "end": v(-74.59, 118.82) * mm});
            skLineSegment(sketch, "E20.1.0.3", {"start": v(-74.59, 136.78) * mm, "end": v(-83.57, 127.8) * mm});
            skLineSegment(sketch, "E20.1.1.0", {"start": v(-65.6, 102.9) * mm, "end": v(-74.59, 111.89) * mm});
            skLineSegment(sketch, "E20.1.1.1", {"start": v(-74.59, 93.93) * mm, "end": v(-65.6, 102.9) * mm});
            skLineSegment(sketch, "E20.1.1.2", {"start": v(-83.57, 102.9) * mm, "end": v(-74.59, 93.93) * mm});
            skLineSegment(sketch, "E20.1.1.3", {"start": v(-74.59, 111.89) * mm, "end": v(-83.57, 102.9) * mm});
            skLineSegment(sketch, "E20.1.2.0", {"start": v(-65.6, 78.01) * mm, "end": v(-74.59, 87) * mm});
            skLineSegment(sketch, "E20.1.2.1", {"start": v(-74.59, 69.03) * mm, "end": v(-65.6, 78.01) * mm});
            skLineSegment(sketch, "E20.1.2.2", {"start": v(-83.57, 78.01) * mm, "end": v(-74.59, 69.03) * mm});
            skLineSegment(sketch, "E20.1.2.3", {"start": v(-74.59, 87) * mm, "end": v(-83.57, 78.01) * mm});
            skLineSegment(sketch, "E20.1.3.0", {"start": v(-65.6, 53.12) * mm, "end": v(-74.59, 62.1) * mm});
            skLineSegment(sketch, "E20.1.3.1", {"start": v(-74.59, 44.14) * mm, "end": v(-65.6, 53.12) * mm});
            skLineSegment(sketch, "E20.1.3.2", {"start": v(-83.57, 53.12) * mm, "end": v(-74.59, 44.14) * mm});
            skLineSegment(sketch, "E20.1.3.3", {"start": v(-74.59, 62.1) * mm, "end": v(-83.57, 53.12) * mm});
            skLineSegment(sketch, "E20.1.4.0", {"start": v(-65.6, 28.23) * mm, "end": v(-74.59, 37.21) * mm});
            skLineSegment(sketch, "E20.1.4.1", {"start": v(-74.59, 19.25) * mm, "end": v(-65.6, 28.23) * mm});
            skLineSegment(sketch, "E20.1.4.2", {"start": v(-83.57, 28.23) * mm, "end": v(-74.59, 19.25) * mm});
            skLineSegment(sketch, "E20.1.4.3", {"start": v(-74.59, 37.21) * mm, "end": v(-83.57, 28.23) * mm});
            skLineSegment(sketch, "E20.2.0.0", {"start": v(-40.97, 127.8) * mm, "end": v(-49.95, 136.78) * mm});
            skLineSegment(sketch, "E20.2.0.1", {"start": v(-49.95, 118.82) * mm, "end": v(-40.97, 127.8) * mm});
            skLineSegment(sketch, "E20.2.0.2", {"start": v(-58.93, 127.8) * mm, "end": v(-49.95, 118.82) * mm});
            skLineSegment(sketch, "E20.2.0.3", {"start": v(-49.95, 136.78) * mm, "end": v(-58.93, 127.8) * mm});
            skLineSegment(sketch, "E20.2.1.0", {"start": v(-40.97, 102.9) * mm, "end": v(-49.95, 111.89) * mm});
            skLineSegment(sketch, "E20.2.1.1", {"start": v(-49.95, 93.93) * mm, "end": v(-40.97, 102.9) * mm});
            skLineSegment(sketch, "E20.2.1.2", {"start": v(-58.93, 102.9) * mm, "end": v(-49.95, 93.93) * mm});
            skLineSegment(sketch, "E20.2.1.3", {"start": v(-49.95, 111.89) * mm, "end": v(-58.93, 102.9) * mm});
            skLineSegment(sketch, "E20.2.2.0", {"start": v(-40.97, 78.01) * mm, "end": v(-49.95, 87) * mm});
            skLineSegment(sketch, "E20.2.2.1", {"start": v(-49.95, 69.03) * mm, "end": v(-40.97, 78.01) * mm});
            skLineSegment(sketch, "E20.2.2.2", {"start": v(-58.93, 78.01) * mm, "end": v(-49.95, 69.03) * mm});
            skLineSegment(sketch, "E20.2.2.3", {"start": v(-49.95, 87) * mm, "end": v(-58.93, 78.01) * mm});
            skLineSegment(sketch, "E20.2.3.0", {"start": v(-40.97, 53.12) * mm, "end": v(-49.95, 62.1) * mm});
            skLineSegment(sketch, "E20.2.3.1", {"start": v(-49.95, 44.14) * mm, "end": v(-40.97, 53.12) * mm});
            skLineSegment(sketch, "E20.2.3.2", {"start": v(-58.93, 53.12) * mm, "end": v(-49.95, 44.14) * mm});
            skLineSegment(sketch, "E20.2.3.3", {"start": v(-49.95, 62.1) * mm, "end": v(-58.93, 53.12) * mm});
            skLineSegment(sketch, "E20.2.4.0", {"start": v(-40.97, 28.23) * mm, "end": v(-49.95, 37.21) * mm});
            skLineSegment(sketch, "E20.2.4.1", {"start": v(-49.95, 19.25) * mm, "end": v(-40.97, 28.23) * mm});
            skLineSegment(sketch, "E20.2.4.2", {"start": v(-58.93, 28.23) * mm, "end": v(-49.95, 19.25) * mm});
            skLineSegment(sketch, "E20.2.4.3", {"start": v(-49.95, 37.21) * mm, "end": v(-58.93, 28.23) * mm});
            skLineSegment(sketch, "E20.3.0.0", {"start": v(-16.33, 127.8) * mm, "end": v(-25.3, 136.78) * mm});
            skLineSegment(sketch, "E20.3.0.1", {"start": v(-25.3, 118.82) * mm, "end": v(-16.33, 127.8) * mm});
            skLineSegment(sketch, "E20.3.0.2", {"start": v(-34.3, 127.8) * mm, "end": v(-25.3, 118.82) * mm});
            skLineSegment(sketch, "E20.3.0.3", {"start": v(-25.3, 136.78) * mm, "end": v(-34.3, 127.8) * mm});
            skLineSegment(sketch, "E20.3.1.0", {"start": v(-16.33, 102.9) * mm, "end": v(-25.3, 111.89) * mm});
            skLineSegment(sketch, "E20.3.1.1", {"start": v(-25.3, 93.93) * mm, "end": v(-16.33, 102.9) * mm});
            skLineSegment(sketch, "E20.3.1.2", {"start": v(-34.3, 102.9) * mm, "end": v(-25.3, 93.93) * mm});
            skLineSegment(sketch, "E20.3.1.3", {"start": v(-25.3, 111.89) * mm, "end": v(-34.3, 102.9) * mm});
            skLineSegment(sketch, "E20.3.2.0", {"start": v(-16.33, 78.01) * mm, "end": v(-25.3, 87) * mm});
            skLineSegment(sketch, "E20.3.2.1", {"start": v(-25.3, 69.03) * mm, "end": v(-16.33, 78.01) * mm});
            skLineSegment(sketch, "E20.3.2.2", {"start": v(-34.3, 78.01) * mm, "end": v(-25.3, 69.03) * mm});
            skLineSegment(sketch, "E20.3.2.3", {"start": v(-25.3, 87) * mm, "end": v(-34.3, 78.01) * mm});
            skLineSegment(sketch, "E20.3.3.0", {"start": v(-16.33, 53.12) * mm, "end": v(-25.3, 62.1) * mm});
            skLineSegment(sketch, "E20.3.3.1", {"start": v(-25.3, 44.14) * mm, "end": v(-16.33, 53.12) * mm});
            skLineSegment(sketch, "E20.3.3.2", {"start": v(-34.3, 53.12) * mm, "end": v(-25.3, 44.14) * mm});
            skLineSegment(sketch, "E20.3.3.3", {"start": v(-25.3, 62.1) * mm, "end": v(-34.3, 53.12) * mm});
            skLineSegment(sketch, "E20.3.4.0", {"start": v(-16.33, 28.23) * mm, "end": v(-25.3, 37.21) * mm});
            skLineSegment(sketch, "E20.3.4.1", {"start": v(-25.3, 19.25) * mm, "end": v(-16.33, 28.23) * mm});
            skLineSegment(sketch, "E20.3.4.2", {"start": v(-34.3, 28.23) * mm, "end": v(-25.3, 19.25) * mm});
            skLineSegment(sketch, "E20.3.4.3", {"start": v(-25.3, 37.21) * mm, "end": v(-34.3, 28.23) * mm});
            skLineSegment(sketch, "E20.4.0.0", {"start": v(8.3, 127.8) * mm, "end": v(-0.67, 136.78) * mm});
            skLineSegment(sketch, "E20.4.0.1", {"start": v(-0.67, 118.82) * mm, "end": v(8.3, 127.8) * mm});
            skLineSegment(sketch, "E20.4.0.2", {"start": v(-9.65, 127.8) * mm, "end": v(-0.67, 118.82) * mm});
            skLineSegment(sketch, "E20.4.0.3", {"start": v(-0.67, 136.78) * mm, "end": v(-9.65, 127.8) * mm});
            skLineSegment(sketch, "E20.4.1.0", {"start": v(8.3, 102.9) * mm, "end": v(-0.67, 111.89) * mm});
            skLineSegment(sketch, "E20.4.1.1", {"start": v(-0.67, 93.93) * mm, "end": v(8.3, 102.9) * mm});
            skLineSegment(sketch, "E20.4.1.2", {"start": v(-9.65, 102.9) * mm, "end": v(-0.67, 93.93) * mm});
            skLineSegment(sketch, "E20.4.1.3", {"start": v(-0.67, 111.89) * mm, "end": v(-9.65, 102.9) * mm});
            skLineSegment(sketch, "E20.4.2.0", {"start": v(8.3, 78.01) * mm, "end": v(-0.67, 87) * mm});
            skLineSegment(sketch, "E20.4.2.1", {"start": v(-0.67, 69.03) * mm, "end": v(8.3, 78.01) * mm});
            skLineSegment(sketch, "E20.4.2.2", {"start": v(-9.65, 78.01) * mm, "end": v(-0.67, 69.03) * mm});
            skLineSegment(sketch, "E20.4.2.3", {"start": v(-0.67, 87) * mm, "end": v(-9.65, 78.01) * mm});
            skLineSegment(sketch, "E20.4.3.0", {"start": v(8.3, 53.12) * mm, "end": v(-0.67, 62.1) * mm});
            skLineSegment(sketch, "E20.4.3.1", {"start": v(-0.67, 44.14) * mm, "end": v(8.3, 53.12) * mm});
            skLineSegment(sketch, "E20.4.3.2", {"start": v(-9.65, 53.12) * mm, "end": v(-0.67, 44.14) * mm});
            skLineSegment(sketch, "E20.4.3.3", {"start": v(-0.67, 62.1) * mm, "end": v(-9.65, 53.12) * mm});
            skLineSegment(sketch, "E20.4.4.0", {"start": v(8.3, 28.23) * mm, "end": v(-0.67, 37.21) * mm});
            skLineSegment(sketch, "E20.4.4.1", {"start": v(-0.67, 19.25) * mm, "end": v(8.3, 28.23) * mm});
            skLineSegment(sketch, "E20.4.4.2", {"start": v(-9.65, 28.23) * mm, "end": v(-0.67, 19.25) * mm});
            skLineSegment(sketch, "E20.4.4.3", {"start": v(-0.67, 37.21) * mm, "end": v(-9.65, 28.23) * mm});
            skLineSegment(sketch, "E20.5.0.0", {"start": v(32.95, 127.8) * mm, "end": v(23.97, 136.78) * mm});
            skLineSegment(sketch, "E20.5.0.1", {"start": v(23.97, 118.82) * mm, "end": v(32.95, 127.8) * mm});
            skLineSegment(sketch, "E20.5.0.2", {"start": v(14.99, 127.8) * mm, "end": v(23.97, 118.82) * mm});
            skLineSegment(sketch, "E20.5.0.3", {"start": v(23.97, 136.78) * mm, "end": v(14.99, 127.8) * mm});
            skLineSegment(sketch, "E20.5.1.0", {"start": v(32.95, 102.9) * mm, "end": v(23.97, 111.89) * mm});
            skLineSegment(sketch, "E20.5.1.1", {"start": v(23.97, 93.93) * mm, "end": v(32.95, 102.9) * mm});
            skLineSegment(sketch, "E20.5.1.2", {"start": v(14.99, 102.9) * mm, "end": v(23.97, 93.93) * mm});
            skLineSegment(sketch, "E20.5.1.3", {"start": v(23.97, 111.89) * mm, "end": v(14.99, 102.9) * mm});
            skLineSegment(sketch, "E20.5.2.0", {"start": v(32.95, 78.01) * mm, "end": v(23.97, 87) * mm});
            skLineSegment(sketch, "E20.5.2.1", {"start": v(23.97, 69.03) * mm, "end": v(32.95, 78.01) * mm});
            skLineSegment(sketch, "E20.5.2.2", {"start": v(14.99, 78.01) * mm, "end": v(23.97, 69.03) * mm});
            skLineSegment(sketch, "E20.5.2.3", {"start": v(23.97, 87) * mm, "end": v(14.99, 78.01) * mm});
            skLineSegment(sketch, "E20.5.3.0", {"start": v(32.95, 53.12) * mm, "end": v(23.97, 62.1) * mm});
            skLineSegment(sketch, "E20.5.3.1", {"start": v(23.97, 44.14) * mm, "end": v(32.95, 53.12) * mm});
            skLineSegment(sketch, "E20.5.3.2", {"start": v(14.99, 53.12) * mm, "end": v(23.97, 44.14) * mm});
            skLineSegment(sketch, "E20.5.3.3", {"start": v(23.97, 62.1) * mm, "end": v(14.99, 53.12) * mm});
            skLineSegment(sketch, "E20.5.4.0", {"start": v(32.95, 28.23) * mm, "end": v(23.97, 37.21) * mm});
            skLineSegment(sketch, "E20.5.4.1", {"start": v(23.97, 19.25) * mm, "end": v(32.95, 28.23) * mm});
            skLineSegment(sketch, "E20.5.4.2", {"start": v(14.99, 28.23) * mm, "end": v(23.97, 19.25) * mm});
            skLineSegment(sketch, "E20.5.4.3", {"start": v(23.97, 37.21) * mm, "end": v(14.99, 28.23) * mm});
            skLineSegment(sketch, "E20.6.0.0", {"start": v(57.58, 127.8) * mm, "end": v(48.6, 136.78) * mm});
            skLineSegment(sketch, "E20.6.0.1", {"start": v(48.6, 118.82) * mm, "end": v(57.58, 127.8) * mm});
            skLineSegment(sketch, "E20.6.0.2", {"start": v(39.62, 127.8) * mm, "end": v(48.6, 118.82) * mm});
            skLineSegment(sketch, "E20.6.0.3", {"start": v(48.6, 136.78) * mm, "end": v(39.62, 127.8) * mm});
            skLineSegment(sketch, "E20.6.1.0", {"start": v(57.58, 102.9) * mm, "end": v(48.6, 111.89) * mm});
            skLineSegment(sketch, "E20.6.1.1", {"start": v(48.6, 93.93) * mm, "end": v(57.58, 102.9) * mm});
            skLineSegment(sketch, "E20.6.1.2", {"start": v(39.62, 102.9) * mm, "end": v(48.6, 93.93) * mm});
            skLineSegment(sketch, "E20.6.1.3", {"start": v(48.6, 111.89) * mm, "end": v(39.62, 102.9) * mm});
            skLineSegment(sketch, "E20.6.2.0", {"start": v(57.58, 78.01) * mm, "end": v(48.6, 87) * mm});
            skLineSegment(sketch, "E20.6.2.1", {"start": v(48.6, 69.03) * mm, "end": v(57.58, 78.01) * mm});
            skLineSegment(sketch, "E20.6.2.2", {"start": v(39.62, 78.01) * mm, "end": v(48.6, 69.03) * mm});
            skLineSegment(sketch, "E20.6.2.3", {"start": v(48.6, 87) * mm, "end": v(39.62, 78.01) * mm});
            skLineSegment(sketch, "E20.6.3.0", {"start": v(57.58, 53.12) * mm, "end": v(48.6, 62.1) * mm});
            skLineSegment(sketch, "E20.6.3.1", {"start": v(48.6, 44.14) * mm, "end": v(57.58, 53.12) * mm});
            skLineSegment(sketch, "E20.6.3.2", {"start": v(39.62, 53.12) * mm, "end": v(48.6, 44.14) * mm});
            skLineSegment(sketch, "E20.6.3.3", {"start": v(48.6, 62.1) * mm, "end": v(39.62, 53.12) * mm});
            skLineSegment(sketch, "E20.6.4.0", {"start": v(57.58, 28.23) * mm, "end": v(48.6, 37.21) * mm});
            skLineSegment(sketch, "E20.6.4.1", {"start": v(48.6, 19.25) * mm, "end": v(57.58, 28.23) * mm});
            skLineSegment(sketch, "E20.6.4.2", {"start": v(39.62, 28.23) * mm, "end": v(48.6, 19.25) * mm});
            skLineSegment(sketch, "E20.6.4.3", {"start": v(48.6, 37.21) * mm, "end": v(39.62, 28.23) * mm});
            skLineSegment(sketch, "E20.7.0.0", {"start": v(82.22, 127.8) * mm, "end": v(73.24, 136.78) * mm});
            skLineSegment(sketch, "E20.7.0.1", {"start": v(73.24, 118.82) * mm, "end": v(82.22, 127.8) * mm});
            skLineSegment(sketch, "E20.7.0.2", {"start": v(64.26, 127.8) * mm, "end": v(73.24, 118.82) * mm});
            skLineSegment(sketch, "E20.7.0.3", {"start": v(73.24, 136.78) * mm, "end": v(64.26, 127.8) * mm});
            skLineSegment(sketch, "E20.7.1.0", {"start": v(82.22, 102.9) * mm, "end": v(73.24, 111.89) * mm});
            skLineSegment(sketch, "E20.7.1.1", {"start": v(73.24, 93.93) * mm, "end": v(82.22, 102.9) * mm});
            skLineSegment(sketch, "E20.7.1.2", {"start": v(64.26, 102.9) * mm, "end": v(73.24, 93.93) * mm});
            skLineSegment(sketch, "E20.7.1.3", {"start": v(73.24, 111.89) * mm, "end": v(64.26, 102.9) * mm});
            skLineSegment(sketch, "E20.7.2.0", {"start": v(82.22, 78.01) * mm, "end": v(73.24, 87) * mm});
            skLineSegment(sketch, "E20.7.2.1", {"start": v(73.24, 69.03) * mm, "end": v(82.22, 78.01) * mm});
            skLineSegment(sketch, "E20.7.2.2", {"start": v(64.26, 78.01) * mm, "end": v(73.24, 69.03) * mm});
            skLineSegment(sketch, "E20.7.2.3", {"start": v(73.24, 87) * mm, "end": v(64.26, 78.01) * mm});
            skLineSegment(sketch, "E20.7.3.0", {"start": v(82.22, 53.12) * mm, "end": v(73.24, 62.1) * mm});
            skLineSegment(sketch, "E20.7.3.1", {"start": v(73.24, 44.14) * mm, "end": v(82.22, 53.12) * mm});
            skLineSegment(sketch, "E20.7.3.2", {"start": v(64.26, 53.12) * mm, "end": v(73.24, 44.14) * mm});
            skLineSegment(sketch, "E20.7.3.3", {"start": v(73.24, 62.1) * mm, "end": v(64.26, 53.12) * mm});
            skLineSegment(sketch, "E20.7.4.0", {"start": v(82.22, 28.23) * mm, "end": v(73.24, 37.21) * mm});
            skLineSegment(sketch, "E20.7.4.1", {"start": v(73.24, 19.25) * mm, "end": v(82.22, 28.23) * mm});
            skLineSegment(sketch, "E20.7.4.2", {"start": v(64.26, 28.23) * mm, "end": v(73.24, 19.25) * mm});
            skLineSegment(sketch, "E20.7.4.3", {"start": v(73.24, 37.21) * mm, "end": v(64.26, 28.23) * mm});
            skLineSegment(sketch, "E20.8.0.0", {"start": v(106.86, 127.8) * mm, "end": v(97.88, 136.78) * mm});
            skLineSegment(sketch, "E20.8.0.1", {"start": v(97.88, 118.82) * mm, "end": v(106.86, 127.8) * mm});
            skLineSegment(sketch, "E20.8.0.2", {"start": v(88.9, 127.8) * mm, "end": v(97.88, 118.82) * mm});
            skLineSegment(sketch, "E20.8.0.3", {"start": v(97.88, 136.78) * mm, "end": v(88.9, 127.8) * mm});
            skLineSegment(sketch, "E20.8.1.0", {"start": v(106.86, 102.9) * mm, "end": v(97.88, 111.89) * mm});
            skLineSegment(sketch, "E20.8.1.1", {"start": v(97.88, 93.93) * mm, "end": v(106.86, 102.9) * mm});
            skLineSegment(sketch, "E20.8.1.2", {"start": v(88.9, 102.9) * mm, "end": v(97.88, 93.93) * mm});
            skLineSegment(sketch, "E20.8.1.3", {"start": v(97.88, 111.89) * mm, "end": v(88.9, 102.9) * mm});
            skLineSegment(sketch, "E20.8.2.0", {"start": v(106.86, 78.01) * mm, "end": v(97.88, 87) * mm});
            skLineSegment(sketch, "E20.8.2.1", {"start": v(97.88, 69.03) * mm, "end": v(106.86, 78.01) * mm});
            skLineSegment(sketch, "E20.8.2.2", {"start": v(88.9, 78.01) * mm, "end": v(97.88, 69.03) * mm});
            skLineSegment(sketch, "E20.8.2.3", {"start": v(97.88, 87) * mm, "end": v(88.9, 78.01) * mm});
            skLineSegment(sketch, "E20.8.3.0", {"start": v(106.86, 53.12) * mm, "end": v(97.88, 62.1) * mm});
            skLineSegment(sketch, "E20.8.3.1", {"start": v(97.88, 44.14) * mm, "end": v(106.86, 53.12) * mm});
            skLineSegment(sketch, "E20.8.3.2", {"start": v(88.9, 53.12) * mm, "end": v(97.88, 44.14) * mm});
            skLineSegment(sketch, "E20.8.3.3", {"start": v(97.88, 62.1) * mm, "end": v(88.9, 53.12) * mm});
            skLineSegment(sketch, "E20.8.4.0", {"start": v(106.86, 28.23) * mm, "end": v(97.88, 37.21) * mm});
            skLineSegment(sketch, "E20.8.4.1", {"start": v(97.88, 19.25) * mm, "end": v(106.86, 28.23) * mm});
            skLineSegment(sketch, "E20.8.4.2", {"start": v(88.9, 28.23) * mm, "end": v(97.88, 19.25) * mm});
            skLineSegment(sketch, "E20.8.4.3", {"start": v(97.88, 37.21) * mm, "end": v(88.9, 28.23) * mm});
            skLineSegment(sketch, "E20.direction1", {"start": v(-90.24, 127.8) * mm, "end": v(-65.6, 127.8) * mm, "construction": true});
            skLineSegment(sketch, "E20.direction2", {"start": v(-90.24, 127.8) * mm, "end": v(-90.24, 102.9) * mm, "construction": true});
            skSolve(sketch);
        }
        {
            var Q0;
            Q0 = qSketchRegion(id + "F8", true);
            extrude(context, id + "F9", {"entities" : qUnion([Q0]), "operationType" : NewBodyOperationType.REMOVE, "endBound" : BoundingType.THROUGH_ALL, "oppositeDirection" : true, "depth" : 25.4 * mm});
        }
        {
            var Q0;
            Q0=makeQuery(id+"F3.boolean.opBoolean","MERGE",FACE,{"derivedFrom":[makeQuery(id+"F1.opExtrude","SWEPT_FACE",FACE,{"disambiguationData":[OSD([sQuery(id+"F0.wireOp",EDGE,"E0.bottom")])]}),makeQuery(id+"F3.opExtrude","SWEPT_FACE",FACE,{"disambiguationData":[OSD([sQuery(id+"F2.wireOp",EDGE,"E1.bottom")])]})]});
            var sketch = newSketch(context, id + "F10", { "sketchPlane" : qUnion([Q0])});
            skLineSegment(sketch, "E21", {"start": v(-111.67, 149.23) * mm, "end": v(-120.65, 140.24) * mm});
            skLineSegment(sketch, "E22", {"start": v(-120.65, 140.24) * mm, "end": v(-111.67, 131.26) * mm});
            skLineSegment(sketch, "E23", {"start": v(-111.67, 131.26) * mm, "end": v(-102.69, 140.24) * mm});
            skLineSegment(sketch, "E24", {"start": v(-102.69, 140.24) * mm, "end": v(-111.67, 149.23) * mm});
            skLineSegment(sketch, "E25", {"start": v(-111.67, 131.26) * mm, "end": v(-81.55, 131.26) * mm, "construction": true});
            skLineSegment(sketch, "E26.0.1.0", {"start": v(-111.67, 106.37) * mm, "end": v(-102.69, 115.35) * mm});
            skLineSegment(sketch, "E26.0.1.1", {"start": v(-111.67, 124.33) * mm, "end": v(-120.65, 115.35) * mm});
            skLineSegment(sketch, "E26.0.1.2", {"start": v(-120.65, 115.35) * mm, "end": v(-111.67, 106.37) * mm});
            skLineSegment(sketch, "E26.0.1.3", {"start": v(-102.69, 115.35) * mm, "end": v(-111.67, 124.33) * mm});
            skLineSegment(sketch, "E26.0.2.0", {"start": v(-111.67, 81.48) * mm, "end": v(-102.69, 90.46) * mm});
            skLineSegment(sketch, "E26.0.2.1", {"start": v(-111.67, 99.44) * mm, "end": v(-120.65, 90.46) * mm});
            skLineSegment(sketch, "E26.0.2.2", {"start": v(-120.65, 90.46) * mm, "end": v(-111.67, 81.48) * mm});
            skLineSegment(sketch, "E26.0.2.3", {"start": v(-102.69, 90.46) * mm, "end": v(-111.67, 99.44) * mm});
            skLineSegment(sketch, "E26.0.3.0", {"start": v(-111.67, 56.59) * mm, "end": v(-102.69, 65.57) * mm});
            skLineSegment(sketch, "E26.0.3.1", {"start": v(-111.67, 74.55) * mm, "end": v(-120.65, 65.57) * mm});
            skLineSegment(sketch, "E26.0.3.2", {"start": v(-120.65, 65.57) * mm, "end": v(-111.67, 56.59) * mm});
            skLineSegment(sketch, "E26.0.3.3", {"start": v(-102.69, 65.57) * mm, "end": v(-111.67, 74.55) * mm});
            skLineSegment(sketch, "E26.0.4.0", {"start": v(-111.67, 31.7) * mm, "end": v(-102.69, 40.68) * mm});
            skLineSegment(sketch, "E26.0.4.1", {"start": v(-111.67, 49.66) * mm, "end": v(-120.65, 40.68) * mm});
            skLineSegment(sketch, "E26.0.4.2", {"start": v(-120.65, 40.68) * mm, "end": v(-111.67, 31.7) * mm});
            skLineSegment(sketch, "E26.0.4.3", {"start": v(-102.69, 40.68) * mm, "end": v(-111.67, 49.66) * mm});
            skLineSegment(sketch, "E26.0.5.0", {"start": v(-111.67, 6.8) * mm, "end": v(-102.69, 15.78) * mm});
            skLineSegment(sketch, "E26.0.5.1", {"start": v(-111.67, 24.77) * mm, "end": v(-120.65, 15.78) * mm});
            skLineSegment(sketch, "E26.0.5.2", {"start": v(-120.65, 15.78) * mm, "end": v(-111.67, 6.8) * mm});
            skLineSegment(sketch, "E26.0.5.3", {"start": v(-102.69, 15.78) * mm, "end": v(-111.67, 24.77) * mm});
            skLineSegment(sketch, "E26.1.0.0", {"start": v(-87.03, 131.26) * mm, "end": v(-78.05, 140.24) * mm});
            skLineSegment(sketch, "E26.1.0.1", {"start": v(-87.03, 149.23) * mm, "end": v(-96.01, 140.24) * mm});
            skLineSegment(sketch, "E26.1.0.2", {"start": v(-96.01, 140.24) * mm, "end": v(-87.03, 131.26) * mm});
            skLineSegment(sketch, "E26.1.0.3", {"start": v(-78.05, 140.24) * mm, "end": v(-87.03, 149.23) * mm});
            skLineSegment(sketch, "E26.1.1.0", {"start": v(-87.03, 106.37) * mm, "end": v(-78.05, 115.35) * mm});
            skLineSegment(sketch, "E26.1.1.1", {"start": v(-87.03, 124.33) * mm, "end": v(-96.01, 115.35) * mm});
            skLineSegment(sketch, "E26.1.1.2", {"start": v(-96.01, 115.35) * mm, "end": v(-87.03, 106.37) * mm});
            skLineSegment(sketch, "E26.1.1.3", {"start": v(-78.05, 115.35) * mm, "end": v(-87.03, 124.33) * mm});
            skLineSegment(sketch, "E26.1.2.0", {"start": v(-87.03, 81.48) * mm, "end": v(-78.05, 90.46) * mm});
            skLineSegment(sketch, "E26.1.2.1", {"start": v(-87.03, 99.44) * mm, "end": v(-96.01, 90.46) * mm});
            skLineSegment(sketch, "E26.1.2.2", {"start": v(-96.01, 90.46) * mm, "end": v(-87.03, 81.48) * mm});
            skLineSegment(sketch, "E26.1.2.3", {"start": v(-78.05, 90.46) * mm, "end": v(-87.03, 99.44) * mm});
            skLineSegment(sketch, "E26.1.3.0", {"start": v(-87.03, 56.59) * mm, "end": v(-78.05, 65.57) * mm});
            skLineSegment(sketch, "E26.1.3.1", {"start": v(-87.03, 74.55) * mm, "end": v(-96.01, 65.57) * mm});
            skLineSegment(sketch, "E26.1.3.2", {"start": v(-96.01, 65.57) * mm, "end": v(-87.03, 56.59) * mm});
            skLineSegment(sketch, "E26.1.3.3", {"start": v(-78.05, 65.57) * mm, "end": v(-87.03, 74.55) * mm});
            skLineSegment(sketch, "E26.1.4.0", {"start": v(-87.03, 31.7) * mm, "end": v(-78.05, 40.68) * mm});
            skLineSegment(sketch, "E26.1.4.1", {"start": v(-87.03, 49.66) * mm, "end": v(-96.01, 40.68) * mm});
            skLineSegment(sketch, "E26.1.4.2", {"start": v(-96.01, 40.68) * mm, "end": v(-87.03, 31.7) * mm});
            skLineSegment(sketch, "E26.1.4.3", {"start": v(-78.05, 40.68) * mm, "end": v(-87.03, 49.66) * mm});
            skLineSegment(sketch, "E26.1.5.0", {"start": v(-87.03, 6.8) * mm, "end": v(-78.05, 15.78) * mm});
            skLineSegment(sketch, "E26.1.5.1", {"start": v(-87.03, 24.77) * mm, "end": v(-96.01, 15.78) * mm});
            skLineSegment(sketch, "E26.1.5.2", {"start": v(-96.01, 15.78) * mm, "end": v(-87.03, 6.8) * mm});
            skLineSegment(sketch, "E26.1.5.3", {"start": v(-78.05, 15.78) * mm, "end": v(-87.03, 24.77) * mm});
            skLineSegment(sketch, "E26.2.0.0", {"start": v(-62.4, 131.26) * mm, "end": v(-53.41, 140.24) * mm});
            skLineSegment(sketch, "E26.2.0.1", {"start": v(-62.4, 149.23) * mm, "end": v(-71.37, 140.24) * mm});
            skLineSegment(sketch, "E26.2.0.2", {"start": v(-71.37, 140.24) * mm, "end": v(-62.4, 131.26) * mm});
            skLineSegment(sketch, "E26.2.0.3", {"start": v(-53.41, 140.24) * mm, "end": v(-62.4, 149.23) * mm});
            skLineSegment(sketch, "E26.2.1.0", {"start": v(-62.4, 106.37) * mm, "end": v(-53.41, 115.35) * mm});
            skLineSegment(sketch, "E26.2.1.1", {"start": v(-62.4, 124.33) * mm, "end": v(-71.37, 115.35) * mm});
            skLineSegment(sketch, "E26.2.1.2", {"start": v(-71.37, 115.35) * mm, "end": v(-62.4, 106.37) * mm});
            skLineSegment(sketch, "E26.2.1.3", {"start": v(-53.41, 115.35) * mm, "end": v(-62.4, 124.33) * mm});
            skLineSegment(sketch, "E26.2.2.0", {"start": v(-62.4, 81.48) * mm, "end": v(-53.41, 90.46) * mm});
            skLineSegment(sketch, "E26.2.2.1", {"start": v(-62.4, 99.44) * mm, "end": v(-71.37, 90.46) * mm});
            skLineSegment(sketch, "E26.2.2.2", {"start": v(-71.37, 90.46) * mm, "end": v(-62.4, 81.48) * mm});
            skLineSegment(sketch, "E26.2.2.3", {"start": v(-53.41, 90.46) * mm, "end": v(-62.4, 99.44) * mm});
            skLineSegment(sketch, "E26.2.3.0", {"start": v(-62.4, 56.59) * mm, "end": v(-53.41, 65.57) * mm});
            skLineSegment(sketch, "E26.2.3.1", {"start": v(-62.4, 74.55) * mm, "end": v(-71.37, 65.57) * mm});
            skLineSegment(sketch, "E26.2.3.2", {"start": v(-71.37, 65.57) * mm, "end": v(-62.4, 56.59) * mm});
            skLineSegment(sketch, "E26.2.3.3", {"start": v(-53.41, 65.57) * mm, "end": v(-62.4, 74.55) * mm});
            skLineSegment(sketch, "E26.2.4.0", {"start": v(-62.4, 31.7) * mm, "end": v(-53.41, 40.68) * mm});
            skLineSegment(sketch, "E26.2.4.1", {"start": v(-62.4, 49.66) * mm, "end": v(-71.37, 40.68) * mm});
            skLineSegment(sketch, "E26.2.4.2", {"start": v(-71.37, 40.68) * mm, "end": v(-62.4, 31.7) * mm});
            skLineSegment(sketch, "E26.2.4.3", {"start": v(-53.41, 40.68) * mm, "end": v(-62.4, 49.66) * mm});
            skLineSegment(sketch, "E26.2.5.0", {"start": v(-62.4, 6.8) * mm, "end": v(-53.41, 15.78) * mm});
            skLineSegment(sketch, "E26.2.5.1", {"start": v(-62.4, 24.77) * mm, "end": v(-71.37, 15.78) * mm});
            skLineSegment(sketch, "E26.2.5.2", {"start": v(-71.37, 15.78) * mm, "end": v(-62.4, 6.8) * mm});
            skLineSegment(sketch, "E26.2.5.3", {"start": v(-53.41, 15.78) * mm, "end": v(-62.4, 24.77) * mm});
            skLineSegment(sketch, "E26.3.0.0", {"start": v(-37.76, 131.26) * mm, "end": v(-28.78, 140.24) * mm});
            skLineSegment(sketch, "E26.3.0.1", {"start": v(-37.76, 149.23) * mm, "end": v(-46.74, 140.24) * mm});
            skLineSegment(sketch, "E26.3.0.2", {"start": v(-46.74, 140.24) * mm, "end": v(-37.76, 131.26) * mm});
            skLineSegment(sketch, "E26.3.0.3", {"start": v(-28.78, 140.24) * mm, "end": v(-37.76, 149.23) * mm});
            skLineSegment(sketch, "E26.3.1.0", {"start": v(-37.76, 106.37) * mm, "end": v(-28.78, 115.35) * mm});
            skLineSegment(sketch, "E26.3.1.1", {"start": v(-37.76, 124.33) * mm, "end": v(-46.74, 115.35) * mm});
            skLineSegment(sketch, "E26.3.1.2", {"start": v(-46.74, 115.35) * mm, "end": v(-37.76, 106.37) * mm});
            skLineSegment(sketch, "E26.3.1.3", {"start": v(-28.78, 115.35) * mm, "end": v(-37.76, 124.33) * mm});
            skLineSegment(sketch, "E26.3.2.0", {"start": v(-37.76, 81.48) * mm, "end": v(-28.78, 90.46) * mm});
            skLineSegment(sketch, "E26.3.2.1", {"start": v(-37.76, 99.44) * mm, "end": v(-46.74, 90.46) * mm});
            skLineSegment(sketch, "E26.3.2.2", {"start": v(-46.74, 90.46) * mm, "end": v(-37.76, 81.48) * mm});
            skLineSegment(sketch, "E26.3.2.3", {"start": v(-28.78, 90.46) * mm, "end": v(-37.76, 99.44) * mm});
            skLineSegment(sketch, "E26.3.3.0", {"start": v(-37.76, 56.59) * mm, "end": v(-28.78, 65.57) * mm});
            skLineSegment(sketch, "E26.3.3.1", {"start": v(-37.76, 74.55) * mm, "end": v(-46.74, 65.57) * mm});
            skLineSegment(sketch, "E26.3.3.2", {"start": v(-46.74, 65.57) * mm, "end": v(-37.76, 56.59) * mm});
            skLineSegment(sketch, "E26.3.3.3", {"start": v(-28.78, 65.57) * mm, "end": v(-37.76, 74.55) * mm});
            skLineSegment(sketch, "E26.3.4.0", {"start": v(-37.76, 31.7) * mm, "end": v(-28.78, 40.68) * mm});
            skLineSegment(sketch, "E26.3.4.1", {"start": v(-37.76, 49.66) * mm, "end": v(-46.74, 40.68) * mm});
            skLineSegment(sketch, "E26.3.4.2", {"start": v(-46.74, 40.68) * mm, "end": v(-37.76, 31.7) * mm});
            skLineSegment(sketch, "E26.3.4.3", {"start": v(-28.78, 40.68) * mm, "end": v(-37.76, 49.66) * mm});
            skLineSegment(sketch, "E26.3.5.0", {"start": v(-37.76, 6.8) * mm, "end": v(-28.78, 15.78) * mm});
            skLineSegment(sketch, "E26.3.5.1", {"start": v(-37.76, 24.77) * mm, "end": v(-46.74, 15.78) * mm});
            skLineSegment(sketch, "E26.3.5.2", {"start": v(-46.74, 15.78) * mm, "end": v(-37.76, 6.8) * mm});
            skLineSegment(sketch, "E26.3.5.3", {"start": v(-28.78, 15.78) * mm, "end": v(-37.76, 24.77) * mm});
            skLineSegment(sketch, "E26.4.0.0", {"start": v(-13.12, 131.26) * mm, "end": v(-4.14, 140.24) * mm});
            skLineSegment(sketch, "E26.4.0.1", {"start": v(-13.12, 149.23) * mm, "end": v(-22.1, 140.24) * mm});
            skLineSegment(sketch, "E26.4.0.2", {"start": v(-22.1, 140.24) * mm, "end": v(-13.12, 131.26) * mm});
            skLineSegment(sketch, "E26.4.0.3", {"start": v(-4.14, 140.24) * mm, "end": v(-13.12, 149.23) * mm});
            skLineSegment(sketch, "E26.4.1.0", {"start": v(-13.12, 106.37) * mm, "end": v(-4.14, 115.35) * mm});
            skLineSegment(sketch, "E26.4.1.1", {"start": v(-13.12, 124.33) * mm, "end": v(-22.1, 115.35) * mm});
            skLineSegment(sketch, "E26.4.1.2", {"start": v(-22.1, 115.35) * mm, "end": v(-13.12, 106.37) * mm});
            skLineSegment(sketch, "E26.4.1.3", {"start": v(-4.14, 115.35) * mm, "end": v(-13.12, 124.33) * mm});
            skLineSegment(sketch, "E26.4.2.0", {"start": v(-13.12, 81.48) * mm, "end": v(-4.14, 90.46) * mm});
            skLineSegment(sketch, "E26.4.2.1", {"start": v(-13.12, 99.44) * mm, "end": v(-22.1, 90.46) * mm});
            skLineSegment(sketch, "E26.4.2.2", {"start": v(-22.1, 90.46) * mm, "end": v(-13.12, 81.48) * mm});
            skLineSegment(sketch, "E26.4.2.3", {"start": v(-4.14, 90.46) * mm, "end": v(-13.12, 99.44) * mm});
            skLineSegment(sketch, "E26.4.3.0", {"start": v(-13.12, 56.59) * mm, "end": v(-4.14, 65.57) * mm});
            skLineSegment(sketch, "E26.4.3.1", {"start": v(-13.12, 74.55) * mm, "end": v(-22.1, 65.57) * mm});
            skLineSegment(sketch, "E26.4.3.2", {"start": v(-22.1, 65.57) * mm, "end": v(-13.12, 56.59) * mm});
            skLineSegment(sketch, "E26.4.3.3", {"start": v(-4.14, 65.57) * mm, "end": v(-13.12, 74.55) * mm});
            skLineSegment(sketch, "E26.4.4.0", {"start": v(-13.12, 31.7) * mm, "end": v(-4.14, 40.68) * mm});
            skLineSegment(sketch, "E26.4.4.1", {"start": v(-13.12, 49.66) * mm, "end": v(-22.1, 40.68) * mm});
            skLineSegment(sketch, "E26.4.4.2", {"start": v(-22.1, 40.68) * mm, "end": v(-13.12, 31.7) * mm});
            skLineSegment(sketch, "E26.4.4.3", {"start": v(-4.14, 40.68) * mm, "end": v(-13.12, 49.66) * mm});
            skLineSegment(sketch, "E26.4.5.0", {"start": v(-13.12, 6.8) * mm, "end": v(-4.14, 15.78) * mm});
            skLineSegment(sketch, "E26.4.5.1", {"start": v(-13.12, 24.77) * mm, "end": v(-22.1, 15.78) * mm});
            skLineSegment(sketch, "E26.4.5.2", {"start": v(-22.1, 15.78) * mm, "end": v(-13.12, 6.8) * mm});
            skLineSegment(sketch, "E26.4.5.3", {"start": v(-4.14, 15.78) * mm, "end": v(-13.12, 24.77) * mm});
            skLineSegment(sketch, "E26.5.0.0", {"start": v(11.52, 131.26) * mm, "end": v(20.5, 140.24) * mm});
            skLineSegment(sketch, "E26.5.0.1", {"start": v(11.52, 149.23) * mm, "end": v(2.54, 140.24) * mm});
            skLineSegment(sketch, "E26.5.0.2", {"start": v(2.54, 140.24) * mm, "end": v(11.52, 131.26) * mm});
            skLineSegment(sketch, "E26.5.0.3", {"start": v(20.5, 140.24) * mm, "end": v(11.52, 149.23) * mm});
            skLineSegment(sketch, "E26.5.1.0", {"start": v(11.52, 106.37) * mm, "end": v(20.5, 115.35) * mm});
            skLineSegment(sketch, "E26.5.1.1", {"start": v(11.52, 124.33) * mm, "end": v(2.54, 115.35) * mm});
            skLineSegment(sketch, "E26.5.1.2", {"start": v(2.54, 115.35) * mm, "end": v(11.52, 106.37) * mm});
            skLineSegment(sketch, "E26.5.1.3", {"start": v(20.5, 115.35) * mm, "end": v(11.52, 124.33) * mm});
            skLineSegment(sketch, "E26.5.2.0", {"start": v(11.52, 81.48) * mm, "end": v(20.5, 90.46) * mm});
            skLineSegment(sketch, "E26.5.2.1", {"start": v(11.52, 99.44) * mm, "end": v(2.54, 90.46) * mm});
            skLineSegment(sketch, "E26.5.2.2", {"start": v(2.54, 90.46) * mm, "end": v(11.52, 81.48) * mm});
            skLineSegment(sketch, "E26.5.2.3", {"start": v(20.5, 90.46) * mm, "end": v(11.52, 99.44) * mm});
            skLineSegment(sketch, "E26.5.3.0", {"start": v(11.52, 56.59) * mm, "end": v(20.5, 65.57) * mm});
            skLineSegment(sketch, "E26.5.3.1", {"start": v(11.52, 74.55) * mm, "end": v(2.54, 65.57) * mm});
            skLineSegment(sketch, "E26.5.3.2", {"start": v(2.54, 65.57) * mm, "end": v(11.52, 56.59) * mm});
            skLineSegment(sketch, "E26.5.3.3", {"start": v(20.5, 65.57) * mm, "end": v(11.52, 74.55) * mm});
            skLineSegment(sketch, "E26.5.4.0", {"start": v(11.52, 31.7) * mm, "end": v(20.5, 40.68) * mm});
            skLineSegment(sketch, "E26.5.4.1", {"start": v(11.52, 49.66) * mm, "end": v(2.54, 40.68) * mm});
            skLineSegment(sketch, "E26.5.4.2", {"start": v(2.54, 40.68) * mm, "end": v(11.52, 31.7) * mm});
            skLineSegment(sketch, "E26.5.4.3", {"start": v(20.5, 40.68) * mm, "end": v(11.52, 49.66) * mm});
            skLineSegment(sketch, "E26.5.5.0", {"start": v(11.52, 6.8) * mm, "end": v(20.5, 15.78) * mm});
            skLineSegment(sketch, "E26.5.5.1", {"start": v(11.52, 24.77) * mm, "end": v(2.54, 15.78) * mm});
            skLineSegment(sketch, "E26.5.5.2", {"start": v(2.54, 15.78) * mm, "end": v(11.52, 6.8) * mm});
            skLineSegment(sketch, "E26.5.5.3", {"start": v(20.5, 15.78) * mm, "end": v(11.52, 24.77) * mm});
            skLineSegment(sketch, "E26.6.0.0", {"start": v(36.16, 131.26) * mm, "end": v(45.14, 140.24) * mm});
            skLineSegment(sketch, "E26.6.0.1", {"start": v(36.16, 149.23) * mm, "end": v(27.18, 140.24) * mm});
            skLineSegment(sketch, "E26.6.0.2", {"start": v(27.18, 140.24) * mm, "end": v(36.16, 131.26) * mm});
            skLineSegment(sketch, "E26.6.0.3", {"start": v(45.14, 140.24) * mm, "end": v(36.16, 149.23) * mm});
            skLineSegment(sketch, "E26.6.1.0", {"start": v(36.16, 106.37) * mm, "end": v(45.14, 115.35) * mm});
            skLineSegment(sketch, "E26.6.1.1", {"start": v(36.16, 124.33) * mm, "end": v(27.18, 115.35) * mm});
            skLineSegment(sketch, "E26.6.1.2", {"start": v(27.18, 115.35) * mm, "end": v(36.16, 106.37) * mm});
            skLineSegment(sketch, "E26.6.1.3", {"start": v(45.14, 115.35) * mm, "end": v(36.16, 124.33) * mm});
            skLineSegment(sketch, "E26.6.2.0", {"start": v(36.16, 81.48) * mm, "end": v(45.14, 90.46) * mm});
            skLineSegment(sketch, "E26.6.2.1", {"start": v(36.16, 99.44) * mm, "end": v(27.18, 90.46) * mm});
            skLineSegment(sketch, "E26.6.2.2", {"start": v(27.18, 90.46) * mm, "end": v(36.16, 81.48) * mm});
            skLineSegment(sketch, "E26.6.2.3", {"start": v(45.14, 90.46) * mm, "end": v(36.16, 99.44) * mm});
            skLineSegment(sketch, "E26.6.3.0", {"start": v(36.16, 56.59) * mm, "end": v(45.14, 65.57) * mm});
            skLineSegment(sketch, "E26.6.3.1", {"start": v(36.16, 74.55) * mm, "end": v(27.18, 65.57) * mm});
            skLineSegment(sketch, "E26.6.3.2", {"start": v(27.18, 65.57) * mm, "end": v(36.16, 56.59) * mm});
            skLineSegment(sketch, "E26.6.3.3", {"start": v(45.14, 65.57) * mm, "end": v(36.16, 74.55) * mm});
            skLineSegment(sketch, "E26.6.4.0", {"start": v(36.16, 31.7) * mm, "end": v(45.14, 40.68) * mm});
            skLineSegment(sketch, "E26.6.4.1", {"start": v(36.16, 49.66) * mm, "end": v(27.18, 40.68) * mm});
            skLineSegment(sketch, "E26.6.4.2", {"start": v(27.18, 40.68) * mm, "end": v(36.16, 31.7) * mm});
            skLineSegment(sketch, "E26.6.4.3", {"start": v(45.14, 40.68) * mm, "end": v(36.16, 49.66) * mm});
            skLineSegment(sketch, "E26.6.5.0", {"start": v(36.16, 6.8) * mm, "end": v(45.14, 15.78) * mm});
            skLineSegment(sketch, "E26.6.5.1", {"start": v(36.16, 24.77) * mm, "end": v(27.18, 15.78) * mm});
            skLineSegment(sketch, "E26.6.5.2", {"start": v(27.18, 15.78) * mm, "end": v(36.16, 6.8) * mm});
            skLineSegment(sketch, "E26.6.5.3", {"start": v(45.14, 15.78) * mm, "end": v(36.16, 24.77) * mm});
            skLineSegment(sketch, "E26.7.0.0", {"start": v(60.8, 131.26) * mm, "end": v(69.78, 140.24) * mm});
            skLineSegment(sketch, "E26.7.0.1", {"start": v(60.8, 149.23) * mm, "end": v(51.82, 140.24) * mm});
            skLineSegment(sketch, "E26.7.0.2", {"start": v(51.82, 140.24) * mm, "end": v(60.8, 131.26) * mm});
            skLineSegment(sketch, "E26.7.0.3", {"start": v(69.78, 140.24) * mm, "end": v(60.8, 149.23) * mm});
            skLineSegment(sketch, "E26.7.1.0", {"start": v(60.8, 106.37) * mm, "end": v(69.78, 115.35) * mm});
            skLineSegment(sketch, "E26.7.1.1", {"start": v(60.8, 124.33) * mm, "end": v(51.82, 115.35) * mm});
            skLineSegment(sketch, "E26.7.1.2", {"start": v(51.82, 115.35) * mm, "end": v(60.8, 106.37) * mm});
            skLineSegment(sketch, "E26.7.1.3", {"start": v(69.78, 115.35) * mm, "end": v(60.8, 124.33) * mm});
            skLineSegment(sketch, "E26.7.2.0", {"start": v(60.8, 81.48) * mm, "end": v(69.78, 90.46) * mm});
            skLineSegment(sketch, "E26.7.2.1", {"start": v(60.8, 99.44) * mm, "end": v(51.82, 90.46) * mm});
            skLineSegment(sketch, "E26.7.2.2", {"start": v(51.82, 90.46) * mm, "end": v(60.8, 81.48) * mm});
            skLineSegment(sketch, "E26.7.2.3", {"start": v(69.78, 90.46) * mm, "end": v(60.8, 99.44) * mm});
            skLineSegment(sketch, "E26.7.3.0", {"start": v(60.8, 56.59) * mm, "end": v(69.78, 65.57) * mm});
            skLineSegment(sketch, "E26.7.3.1", {"start": v(60.8, 74.55) * mm, "end": v(51.82, 65.57) * mm});
            skLineSegment(sketch, "E26.7.3.2", {"start": v(51.82, 65.57) * mm, "end": v(60.8, 56.59) * mm});
            skLineSegment(sketch, "E26.7.3.3", {"start": v(69.78, 65.57) * mm, "end": v(60.8, 74.55) * mm});
            skLineSegment(sketch, "E26.7.4.0", {"start": v(60.8, 31.7) * mm, "end": v(69.78, 40.68) * mm});
            skLineSegment(sketch, "E26.7.4.1", {"start": v(60.8, 49.66) * mm, "end": v(51.82, 40.68) * mm});
            skLineSegment(sketch, "E26.7.4.2", {"start": v(51.82, 40.68) * mm, "end": v(60.8, 31.7) * mm});
            skLineSegment(sketch, "E26.7.4.3", {"start": v(69.78, 40.68) * mm, "end": v(60.8, 49.66) * mm});
            skLineSegment(sketch, "E26.7.5.0", {"start": v(60.8, 6.8) * mm, "end": v(69.78, 15.78) * mm});
            skLineSegment(sketch, "E26.7.5.1", {"start": v(60.8, 24.77) * mm, "end": v(51.82, 15.78) * mm});
            skLineSegment(sketch, "E26.7.5.2", {"start": v(51.82, 15.78) * mm, "end": v(60.8, 6.8) * mm});
            skLineSegment(sketch, "E26.7.5.3", {"start": v(69.78, 15.78) * mm, "end": v(60.8, 24.77) * mm});
            skLineSegment(sketch, "E26.8.0.0", {"start": v(85.43, 131.26) * mm, "end": v(94.41, 140.24) * mm});
            skLineSegment(sketch, "E26.8.0.1", {"start": v(85.43, 149.23) * mm, "end": v(76.45, 140.24) * mm});
            skLineSegment(sketch, "E26.8.0.2", {"start": v(76.45, 140.24) * mm, "end": v(85.43, 131.26) * mm});
            skLineSegment(sketch, "E26.8.0.3", {"start": v(94.41, 140.24) * mm, "end": v(85.43, 149.23) * mm});
            skLineSegment(sketch, "E26.8.1.0", {"start": v(85.43, 106.37) * mm, "end": v(94.41, 115.35) * mm});
            skLineSegment(sketch, "E26.8.1.1", {"start": v(85.43, 124.33) * mm, "end": v(76.45, 115.35) * mm});
            skLineSegment(sketch, "E26.8.1.2", {"start": v(76.45, 115.35) * mm, "end": v(85.43, 106.37) * mm});
            skLineSegment(sketch, "E26.8.1.3", {"start": v(94.41, 115.35) * mm, "end": v(85.43, 124.33) * mm});
            skLineSegment(sketch, "E26.8.2.0", {"start": v(85.43, 81.48) * mm, "end": v(94.41, 90.46) * mm});
            skLineSegment(sketch, "E26.8.2.1", {"start": v(85.43, 99.44) * mm, "end": v(76.45, 90.46) * mm});
            skLineSegment(sketch, "E26.8.2.2", {"start": v(76.45, 90.46) * mm, "end": v(85.43, 81.48) * mm});
            skLineSegment(sketch, "E26.8.2.3", {"start": v(94.41, 90.46) * mm, "end": v(85.43, 99.44) * mm});
            skLineSegment(sketch, "E26.8.3.0", {"start": v(85.43, 56.59) * mm, "end": v(94.41, 65.57) * mm});
            skLineSegment(sketch, "E26.8.3.1", {"start": v(85.43, 74.55) * mm, "end": v(76.45, 65.57) * mm});
            skLineSegment(sketch, "E26.8.3.2", {"start": v(76.45, 65.57) * mm, "end": v(85.43, 56.59) * mm});
            skLineSegment(sketch, "E26.8.3.3", {"start": v(94.41, 65.57) * mm, "end": v(85.43, 74.55) * mm});
            skLineSegment(sketch, "E26.8.4.0", {"start": v(85.43, 31.7) * mm, "end": v(94.41, 40.68) * mm});
            skLineSegment(sketch, "E26.8.4.1", {"start": v(85.43, 49.66) * mm, "end": v(76.45, 40.68) * mm});
            skLineSegment(sketch, "E26.8.4.2", {"start": v(76.45, 40.68) * mm, "end": v(85.43, 31.7) * mm});
            skLineSegment(sketch, "E26.8.4.3", {"start": v(94.41, 40.68) * mm, "end": v(85.43, 49.66) * mm});
            skLineSegment(sketch, "E26.8.5.0", {"start": v(85.43, 6.8) * mm, "end": v(94.41, 15.78) * mm});
            skLineSegment(sketch, "E26.8.5.1", {"start": v(85.43, 24.77) * mm, "end": v(76.45, 15.78) * mm});
            skLineSegment(sketch, "E26.8.5.2", {"start": v(76.45, 15.78) * mm, "end": v(85.43, 6.8) * mm});
            skLineSegment(sketch, "E26.8.5.3", {"start": v(94.41, 15.78) * mm, "end": v(85.43, 24.77) * mm});
            skLineSegment(sketch, "E26.9.0.0", {"start": v(110.07, 131.26) * mm, "end": v(119.05, 140.24) * mm});
            skLineSegment(sketch, "E26.9.0.1", {"start": v(110.07, 149.23) * mm, "end": v(101.1, 140.24) * mm});
            skLineSegment(sketch, "E26.9.0.2", {"start": v(101.1, 140.24) * mm, "end": v(110.07, 131.26) * mm});
            skLineSegment(sketch, "E26.9.0.3", {"start": v(119.05, 140.24) * mm, "end": v(110.07, 149.23) * mm});
            skLineSegment(sketch, "E26.9.1.0", {"start": v(110.07, 106.37) * mm, "end": v(119.05, 115.35) * mm});
            skLineSegment(sketch, "E26.9.1.1", {"start": v(110.07, 124.33) * mm, "end": v(101.1, 115.35) * mm});
            skLineSegment(sketch, "E26.9.1.2", {"start": v(101.1, 115.35) * mm, "end": v(110.07, 106.37) * mm});
            skLineSegment(sketch, "E26.9.1.3", {"start": v(119.05, 115.35) * mm, "end": v(110.07, 124.33) * mm});
            skLineSegment(sketch, "E26.9.2.0", {"start": v(110.07, 81.48) * mm, "end": v(119.05, 90.46) * mm});
            skLineSegment(sketch, "E26.9.2.1", {"start": v(110.07, 99.44) * mm, "end": v(101.1, 90.46) * mm});
            skLineSegment(sketch, "E26.9.2.2", {"start": v(101.1, 90.46) * mm, "end": v(110.07, 81.48) * mm});
            skLineSegment(sketch, "E26.9.2.3", {"start": v(119.05, 90.46) * mm, "end": v(110.07, 99.44) * mm});
            skLineSegment(sketch, "E26.9.3.0", {"start": v(110.07, 56.59) * mm, "end": v(119.05, 65.57) * mm});
            skLineSegment(sketch, "E26.9.3.1", {"start": v(110.07, 74.55) * mm, "end": v(101.1, 65.57) * mm});
            skLineSegment(sketch, "E26.9.3.2", {"start": v(101.1, 65.57) * mm, "end": v(110.07, 56.59) * mm});
            skLineSegment(sketch, "E26.9.3.3", {"start": v(119.05, 65.57) * mm, "end": v(110.07, 74.55) * mm});
            skLineSegment(sketch, "E26.9.4.0", {"start": v(110.07, 31.7) * mm, "end": v(119.05, 40.68) * mm});
            skLineSegment(sketch, "E26.9.4.1", {"start": v(110.07, 49.66) * mm, "end": v(101.1, 40.68) * mm});
            skLineSegment(sketch, "E26.9.4.2", {"start": v(101.1, 40.68) * mm, "end": v(110.07, 31.7) * mm});
            skLineSegment(sketch, "E26.9.4.3", {"start": v(119.05, 40.68) * mm, "end": v(110.07, 49.66) * mm});
            skLineSegment(sketch, "E26.9.5.0", {"start": v(110.07, 6.8) * mm, "end": v(119.05, 15.78) * mm});
            skLineSegment(sketch, "E26.9.5.1", {"start": v(110.07, 24.77) * mm, "end": v(101.1, 15.78) * mm});
            skLineSegment(sketch, "E26.9.5.2", {"start": v(101.1, 15.78) * mm, "end": v(110.07, 6.8) * mm});
            skLineSegment(sketch, "E26.9.5.3", {"start": v(119.05, 15.78) * mm, "end": v(110.07, 24.77) * mm});
            skLineSegment(sketch, "E26.direction1", {"start": v(-111.67, 131.26) * mm, "end": v(-87.03, 131.26) * mm, "construction": true});
            skLineSegment(sketch, "E26.direction2", {"start": v(-111.67, 131.26) * mm, "end": v(-111.67, 106.37) * mm, "construction": true});
            skSolve(sketch);
        }
        {
            var Q0;
            Q0 = qSketchRegion(id + "F10", true);
            extrude(context, id + "F11", {"entities" : qUnion([Q0]), "operationType" : NewBodyOperationType.REMOVE, "endBound" : BoundingType.THROUGH_ALL, "oppositeDirection" : true, "depth" : 25.4 * mm});
        }
        {
            var Q0;
            Q0=makeQuery(id+"F3.boolean.opBoolean","MERGE",FACE,{"derivedFrom":[makeQuery(id+"F1.opExtrude","SWEPT_FACE",FACE,{"disambiguationData":[OSD([sQuery(id+"F0.wireOp",EDGE,"E0.bottom")])]}),makeQuery(id+"F3.opExtrude","SWEPT_FACE",FACE,{"disambiguationData":[OSD([sQuery(id+"F2.wireOp",EDGE,"E1.bottom")])]})]});
            var sketch = newSketch(context, id + "F12", { "sketchPlane" : qUnion([Q0])});
            skLineSegment(sketch, "E27", {"start": v(-99.22, 136.78) * mm, "end": v(-90.24, 127.8) * mm});
            skLineSegment(sketch, "E28", {"start": v(-90.24, 127.8) * mm, "end": v(-99.22, 118.82) * mm});
            skLineSegment(sketch, "E29", {"start": v(-99.22, 118.82) * mm, "end": v(-108.2, 127.8) * mm});
            skLineSegment(sketch, "E30", {"start": v(-108.2, 127.8) * mm, "end": v(-99.22, 136.78) * mm});
            skLineSegment(sketch, "E31.0.1.0", {"start": v(-108.2, 102.9) * mm, "end": v(-99.22, 111.89) * mm});
            skLineSegment(sketch, "E31.0.1.1", {"start": v(-99.22, 93.93) * mm, "end": v(-108.2, 102.9) * mm});
            skLineSegment(sketch, "E31.0.1.2", {"start": v(-90.24, 102.9) * mm, "end": v(-99.22, 93.93) * mm});
            skLineSegment(sketch, "E31.0.1.3", {"start": v(-99.22, 111.89) * mm, "end": v(-90.24, 102.9) * mm});
            skLineSegment(sketch, "E31.0.2.0", {"start": v(-108.2, 78.01) * mm, "end": v(-99.22, 87) * mm});
            skLineSegment(sketch, "E31.0.2.1", {"start": v(-99.22, 69.03) * mm, "end": v(-108.2, 78.01) * mm});
            skLineSegment(sketch, "E31.0.2.2", {"start": v(-90.24, 78.01) * mm, "end": v(-99.22, 69.03) * mm});
            skLineSegment(sketch, "E31.0.2.3", {"start": v(-99.22, 87) * mm, "end": v(-90.24, 78.01) * mm});
            skLineSegment(sketch, "E31.0.3.0", {"start": v(-108.2, 53.12) * mm, "end": v(-99.22, 62.1) * mm});
            skLineSegment(sketch, "E31.0.3.1", {"start": v(-99.22, 44.14) * mm, "end": v(-108.2, 53.12) * mm});
            skLineSegment(sketch, "E31.0.3.2", {"start": v(-90.24, 53.12) * mm, "end": v(-99.22, 44.14) * mm});
            skLineSegment(sketch, "E31.0.3.3", {"start": v(-99.22, 62.1) * mm, "end": v(-90.24, 53.12) * mm});
            skLineSegment(sketch, "E31.0.4.0", {"start": v(-108.2, 28.23) * mm, "end": v(-99.22, 37.21) * mm});
            skLineSegment(sketch, "E31.0.4.1", {"start": v(-99.22, 19.25) * mm, "end": v(-108.2, 28.23) * mm});
            skLineSegment(sketch, "E31.0.4.2", {"start": v(-90.24, 28.23) * mm, "end": v(-99.22, 19.25) * mm});
            skLineSegment(sketch, "E31.0.4.3", {"start": v(-99.22, 37.21) * mm, "end": v(-90.24, 28.23) * mm});
            skLineSegment(sketch, "E31.1.0.0", {"start": v(-83.57, 127.8) * mm, "end": v(-74.59, 136.78) * mm});
            skLineSegment(sketch, "E31.1.0.1", {"start": v(-74.59, 118.82) * mm, "end": v(-83.57, 127.8) * mm});
            skLineSegment(sketch, "E31.1.0.2", {"start": v(-65.6, 127.8) * mm, "end": v(-74.59, 118.82) * mm});
            skLineSegment(sketch, "E31.1.0.3", {"start": v(-74.59, 136.78) * mm, "end": v(-65.6, 127.8) * mm});
            skLineSegment(sketch, "E31.1.1.0", {"start": v(-83.57, 102.9) * mm, "end": v(-74.59, 111.89) * mm});
            skLineSegment(sketch, "E31.1.1.1", {"start": v(-74.59, 93.93) * mm, "end": v(-83.57, 102.9) * mm});
            skLineSegment(sketch, "E31.1.1.2", {"start": v(-65.6, 102.9) * mm, "end": v(-74.59, 93.93) * mm});
            skLineSegment(sketch, "E31.1.1.3", {"start": v(-74.59, 111.89) * mm, "end": v(-65.6, 102.9) * mm});
            skLineSegment(sketch, "E31.1.2.0", {"start": v(-83.57, 78.01) * mm, "end": v(-74.59, 87) * mm});
            skLineSegment(sketch, "E31.1.2.1", {"start": v(-74.59, 69.03) * mm, "end": v(-83.57, 78.01) * mm});
            skLineSegment(sketch, "E31.1.2.2", {"start": v(-65.6, 78.01) * mm, "end": v(-74.59, 69.03) * mm});
            skLineSegment(sketch, "E31.1.2.3", {"start": v(-74.59, 87) * mm, "end": v(-65.6, 78.01) * mm});
            skLineSegment(sketch, "E31.1.3.0", {"start": v(-83.57, 53.12) * mm, "end": v(-74.59, 62.1) * mm});
            skLineSegment(sketch, "E31.1.3.1", {"start": v(-74.59, 44.14) * mm, "end": v(-83.57, 53.12) * mm});
            skLineSegment(sketch, "E31.1.3.2", {"start": v(-65.6, 53.12) * mm, "end": v(-74.59, 44.14) * mm});
            skLineSegment(sketch, "E31.1.3.3", {"start": v(-74.59, 62.1) * mm, "end": v(-65.6, 53.12) * mm});
            skLineSegment(sketch, "E31.1.4.0", {"start": v(-83.57, 28.23) * mm, "end": v(-74.59, 37.21) * mm});
            skLineSegment(sketch, "E31.1.4.1", {"start": v(-74.59, 19.25) * mm, "end": v(-83.57, 28.23) * mm});
            skLineSegment(sketch, "E31.1.4.2", {"start": v(-65.6, 28.23) * mm, "end": v(-74.59, 19.25) * mm});
            skLineSegment(sketch, "E31.1.4.3", {"start": v(-74.59, 37.21) * mm, "end": v(-65.6, 28.23) * mm});
            skLineSegment(sketch, "E31.2.0.0", {"start": v(-58.93, 127.8) * mm, "end": v(-49.95, 136.78) * mm});
            skLineSegment(sketch, "E31.2.0.1", {"start": v(-49.95, 118.82) * mm, "end": v(-58.93, 127.8) * mm});
            skLineSegment(sketch, "E31.2.0.2", {"start": v(-40.97, 127.8) * mm, "end": v(-49.95, 118.82) * mm});
            skLineSegment(sketch, "E31.2.0.3", {"start": v(-49.95, 136.78) * mm, "end": v(-40.97, 127.8) * mm});
            skLineSegment(sketch, "E31.2.1.0", {"start": v(-58.93, 102.9) * mm, "end": v(-49.95, 111.89) * mm});
            skLineSegment(sketch, "E31.2.1.1", {"start": v(-49.95, 93.93) * mm, "end": v(-58.93, 102.9) * mm});
            skLineSegment(sketch, "E31.2.1.2", {"start": v(-40.97, 102.9) * mm, "end": v(-49.95, 93.93) * mm});
            skLineSegment(sketch, "E31.2.1.3", {"start": v(-49.95, 111.89) * mm, "end": v(-40.97, 102.9) * mm});
            skLineSegment(sketch, "E31.2.2.0", {"start": v(-58.93, 78.01) * mm, "end": v(-49.95, 87) * mm});
            skLineSegment(sketch, "E31.2.2.1", {"start": v(-49.95, 69.03) * mm, "end": v(-58.93, 78.01) * mm});
            skLineSegment(sketch, "E31.2.2.2", {"start": v(-40.97, 78.01) * mm, "end": v(-49.95, 69.03) * mm});
            skLineSegment(sketch, "E31.2.2.3", {"start": v(-49.95, 87) * mm, "end": v(-40.97, 78.01) * mm});
            skLineSegment(sketch, "E31.2.3.0", {"start": v(-58.93, 53.12) * mm, "end": v(-49.95, 62.1) * mm});
            skLineSegment(sketch, "E31.2.3.1", {"start": v(-49.95, 44.14) * mm, "end": v(-58.93, 53.12) * mm});
            skLineSegment(sketch, "E31.2.3.2", {"start": v(-40.97, 53.12) * mm, "end": v(-49.95, 44.14) * mm});
            skLineSegment(sketch, "E31.2.3.3", {"start": v(-49.95, 62.1) * mm, "end": v(-40.97, 53.12) * mm});
            skLineSegment(sketch, "E31.2.4.0", {"start": v(-58.93, 28.23) * mm, "end": v(-49.95, 37.21) * mm});
            skLineSegment(sketch, "E31.2.4.1", {"start": v(-49.95, 19.25) * mm, "end": v(-58.93, 28.23) * mm});
            skLineSegment(sketch, "E31.2.4.2", {"start": v(-40.97, 28.23) * mm, "end": v(-49.95, 19.25) * mm});
            skLineSegment(sketch, "E31.2.4.3", {"start": v(-49.95, 37.21) * mm, "end": v(-40.97, 28.23) * mm});
            skLineSegment(sketch, "E31.3.0.0", {"start": v(-34.3, 127.8) * mm, "end": v(-25.3, 136.78) * mm});
            skLineSegment(sketch, "E31.3.0.1", {"start": v(-25.3, 118.82) * mm, "end": v(-34.3, 127.8) * mm});
            skLineSegment(sketch, "E31.3.0.2", {"start": v(-16.33, 127.8) * mm, "end": v(-25.3, 118.82) * mm});
            skLineSegment(sketch, "E31.3.0.3", {"start": v(-25.3, 136.78) * mm, "end": v(-16.33, 127.8) * mm});
            skLineSegment(sketch, "E31.3.1.0", {"start": v(-34.3, 102.9) * mm, "end": v(-25.3, 111.89) * mm});
            skLineSegment(sketch, "E31.3.1.1", {"start": v(-25.3, 93.93) * mm, "end": v(-34.3, 102.9) * mm});
            skLineSegment(sketch, "E31.3.1.2", {"start": v(-16.33, 102.9) * mm, "end": v(-25.3, 93.93) * mm});
            skLineSegment(sketch, "E31.3.1.3", {"start": v(-25.3, 111.89) * mm, "end": v(-16.33, 102.9) * mm});
            skLineSegment(sketch, "E31.3.2.0", {"start": v(-34.3, 78.01) * mm, "end": v(-25.3, 87) * mm});
            skLineSegment(sketch, "E31.3.2.1", {"start": v(-25.3, 69.03) * mm, "end": v(-34.3, 78.01) * mm});
            skLineSegment(sketch, "E31.3.2.2", {"start": v(-16.33, 78.01) * mm, "end": v(-25.3, 69.03) * mm});
            skLineSegment(sketch, "E31.3.2.3", {"start": v(-25.3, 87) * mm, "end": v(-16.33, 78.01) * mm});
            skLineSegment(sketch, "E31.3.3.0", {"start": v(-34.3, 53.12) * mm, "end": v(-25.3, 62.1) * mm});
            skLineSegment(sketch, "E31.3.3.1", {"start": v(-25.3, 44.14) * mm, "end": v(-34.3, 53.12) * mm});
            skLineSegment(sketch, "E31.3.3.2", {"start": v(-16.33, 53.12) * mm, "end": v(-25.3, 44.14) * mm});
            skLineSegment(sketch, "E31.3.3.3", {"start": v(-25.3, 62.1) * mm, "end": v(-16.33, 53.12) * mm});
            skLineSegment(sketch, "E31.3.4.0", {"start": v(-34.3, 28.23) * mm, "end": v(-25.3, 37.21) * mm});
            skLineSegment(sketch, "E31.3.4.1", {"start": v(-25.3, 19.25) * mm, "end": v(-34.3, 28.23) * mm});
            skLineSegment(sketch, "E31.3.4.2", {"start": v(-16.33, 28.23) * mm, "end": v(-25.3, 19.25) * mm});
            skLineSegment(sketch, "E31.3.4.3", {"start": v(-25.3, 37.21) * mm, "end": v(-16.33, 28.23) * mm});
            skLineSegment(sketch, "E31.4.0.0", {"start": v(-9.65, 127.8) * mm, "end": v(-0.67, 136.78) * mm});
            skLineSegment(sketch, "E31.4.0.1", {"start": v(-0.67, 118.82) * mm, "end": v(-9.65, 127.8) * mm});
            skLineSegment(sketch, "E31.4.0.2", {"start": v(8.3, 127.8) * mm, "end": v(-0.67, 118.82) * mm});
            skLineSegment(sketch, "E31.4.0.3", {"start": v(-0.67, 136.78) * mm, "end": v(8.3, 127.8) * mm});
            skLineSegment(sketch, "E31.4.1.0", {"start": v(-9.65, 102.9) * mm, "end": v(-0.67, 111.89) * mm});
            skLineSegment(sketch, "E31.4.1.1", {"start": v(-0.67, 93.93) * mm, "end": v(-9.65, 102.9) * mm});
            skLineSegment(sketch, "E31.4.1.2", {"start": v(8.3, 102.9) * mm, "end": v(-0.67, 93.93) * mm});
            skLineSegment(sketch, "E31.4.1.3", {"start": v(-0.67, 111.89) * mm, "end": v(8.3, 102.9) * mm});
            skLineSegment(sketch, "E31.4.2.0", {"start": v(-9.65, 78.01) * mm, "end": v(-0.67, 87) * mm});
            skLineSegment(sketch, "E31.4.2.1", {"start": v(-0.67, 69.03) * mm, "end": v(-9.65, 78.01) * mm});
            skLineSegment(sketch, "E31.4.2.2", {"start": v(8.3, 78.01) * mm, "end": v(-0.67, 69.03) * mm});
            skLineSegment(sketch, "E31.4.2.3", {"start": v(-0.67, 87) * mm, "end": v(8.3, 78.01) * mm});
            skLineSegment(sketch, "E31.4.3.0", {"start": v(-9.65, 53.12) * mm, "end": v(-0.67, 62.1) * mm});
            skLineSegment(sketch, "E31.4.3.1", {"start": v(-0.67, 44.14) * mm, "end": v(-9.65, 53.12) * mm});
            skLineSegment(sketch, "E31.4.3.2", {"start": v(8.3, 53.12) * mm, "end": v(-0.67, 44.14) * mm});
            skLineSegment(sketch, "E31.4.3.3", {"start": v(-0.67, 62.1) * mm, "end": v(8.3, 53.12) * mm});
            skLineSegment(sketch, "E31.4.4.0", {"start": v(-9.65, 28.23) * mm, "end": v(-0.67, 37.21) * mm});
            skLineSegment(sketch, "E31.4.4.1", {"start": v(-0.67, 19.25) * mm, "end": v(-9.65, 28.23) * mm});
            skLineSegment(sketch, "E31.4.4.2", {"start": v(8.3, 28.23) * mm, "end": v(-0.67, 19.25) * mm});
            skLineSegment(sketch, "E31.4.4.3", {"start": v(-0.67, 37.21) * mm, "end": v(8.3, 28.23) * mm});
            skLineSegment(sketch, "E31.5.0.0", {"start": v(14.99, 127.8) * mm, "end": v(23.97, 136.78) * mm});
            skLineSegment(sketch, "E31.5.0.1", {"start": v(23.97, 118.82) * mm, "end": v(14.99, 127.8) * mm});
            skLineSegment(sketch, "E31.5.0.2", {"start": v(32.95, 127.8) * mm, "end": v(23.97, 118.82) * mm});
            skLineSegment(sketch, "E31.5.0.3", {"start": v(23.97, 136.78) * mm, "end": v(32.95, 127.8) * mm});
            skLineSegment(sketch, "E31.5.1.0", {"start": v(14.99, 102.9) * mm, "end": v(23.97, 111.89) * mm});
            skLineSegment(sketch, "E31.5.1.1", {"start": v(23.97, 93.93) * mm, "end": v(14.99, 102.9) * mm});
            skLineSegment(sketch, "E31.5.1.2", {"start": v(32.95, 102.9) * mm, "end": v(23.97, 93.93) * mm});
            skLineSegment(sketch, "E31.5.1.3", {"start": v(23.97, 111.89) * mm, "end": v(32.95, 102.9) * mm});
            skLineSegment(sketch, "E31.5.2.0", {"start": v(14.99, 78.01) * mm, "end": v(23.97, 87) * mm});
            skLineSegment(sketch, "E31.5.2.1", {"start": v(23.97, 69.03) * mm, "end": v(14.99, 78.01) * mm});
            skLineSegment(sketch, "E31.5.2.2", {"start": v(32.95, 78.01) * mm, "end": v(23.97, 69.03) * mm});
            skLineSegment(sketch, "E31.5.2.3", {"start": v(23.97, 87) * mm, "end": v(32.95, 78.01) * mm});
            skLineSegment(sketch, "E31.5.3.0", {"start": v(14.99, 53.12) * mm, "end": v(23.97, 62.1) * mm});
            skLineSegment(sketch, "E31.5.3.1", {"start": v(23.97, 44.14) * mm, "end": v(14.99, 53.12) * mm});
            skLineSegment(sketch, "E31.5.3.2", {"start": v(32.95, 53.12) * mm, "end": v(23.97, 44.14) * mm});
            skLineSegment(sketch, "E31.5.3.3", {"start": v(23.97, 62.1) * mm, "end": v(32.95, 53.12) * mm});
            skLineSegment(sketch, "E31.5.4.0", {"start": v(14.99, 28.23) * mm, "end": v(23.97, 37.21) * mm});
            skLineSegment(sketch, "E31.5.4.1", {"start": v(23.97, 19.25) * mm, "end": v(14.99, 28.23) * mm});
            skLineSegment(sketch, "E31.5.4.2", {"start": v(32.95, 28.23) * mm, "end": v(23.97, 19.25) * mm});
            skLineSegment(sketch, "E31.5.4.3", {"start": v(23.97, 37.21) * mm, "end": v(32.95, 28.23) * mm});
            skLineSegment(sketch, "E31.6.0.0", {"start": v(39.62, 127.8) * mm, "end": v(48.6, 136.78) * mm});
            skLineSegment(sketch, "E31.6.0.1", {"start": v(48.6, 118.82) * mm, "end": v(39.62, 127.8) * mm});
            skLineSegment(sketch, "E31.6.0.2", {"start": v(57.58, 127.8) * mm, "end": v(48.6, 118.82) * mm});
            skLineSegment(sketch, "E31.6.0.3", {"start": v(48.6, 136.78) * mm, "end": v(57.58, 127.8) * mm});
            skLineSegment(sketch, "E31.6.1.0", {"start": v(39.62, 102.9) * mm, "end": v(48.6, 111.89) * mm});
            skLineSegment(sketch, "E31.6.1.1", {"start": v(48.6, 93.93) * mm, "end": v(39.62, 102.9) * mm});
            skLineSegment(sketch, "E31.6.1.2", {"start": v(57.58, 102.9) * mm, "end": v(48.6, 93.93) * mm});
            skLineSegment(sketch, "E31.6.1.3", {"start": v(48.6, 111.89) * mm, "end": v(57.58, 102.9) * mm});
            skLineSegment(sketch, "E31.6.2.0", {"start": v(39.62, 78.01) * mm, "end": v(48.6, 87) * mm});
            skLineSegment(sketch, "E31.6.2.1", {"start": v(48.6, 69.03) * mm, "end": v(39.62, 78.01) * mm});
            skLineSegment(sketch, "E31.6.2.2", {"start": v(57.58, 78.01) * mm, "end": v(48.6, 69.03) * mm});
            skLineSegment(sketch, "E31.6.2.3", {"start": v(48.6, 87) * mm, "end": v(57.58, 78.01) * mm});
            skLineSegment(sketch, "E31.6.3.0", {"start": v(39.62, 53.12) * mm, "end": v(48.6, 62.1) * mm});
            skLineSegment(sketch, "E31.6.3.1", {"start": v(48.6, 44.14) * mm, "end": v(39.62, 53.12) * mm});
            skLineSegment(sketch, "E31.6.3.2", {"start": v(57.58, 53.12) * mm, "end": v(48.6, 44.14) * mm});
            skLineSegment(sketch, "E31.6.3.3", {"start": v(48.6, 62.1) * mm, "end": v(57.58, 53.12) * mm});
            skLineSegment(sketch, "E31.6.4.0", {"start": v(39.62, 28.23) * mm, "end": v(48.6, 37.21) * mm});
            skLineSegment(sketch, "E31.6.4.1", {"start": v(48.6, 19.25) * mm, "end": v(39.62, 28.23) * mm});
            skLineSegment(sketch, "E31.6.4.2", {"start": v(57.58, 28.23) * mm, "end": v(48.6, 19.25) * mm});
            skLineSegment(sketch, "E31.6.4.3", {"start": v(48.6, 37.21) * mm, "end": v(57.58, 28.23) * mm});
            skLineSegment(sketch, "E31.7.0.0", {"start": v(64.26, 127.8) * mm, "end": v(73.24, 136.78) * mm});
            skLineSegment(sketch, "E31.7.0.1", {"start": v(73.24, 118.82) * mm, "end": v(64.26, 127.8) * mm});
            skLineSegment(sketch, "E31.7.0.2", {"start": v(82.22, 127.8) * mm, "end": v(73.24, 118.82) * mm});
            skLineSegment(sketch, "E31.7.0.3", {"start": v(73.24, 136.78) * mm, "end": v(82.22, 127.8) * mm});
            skLineSegment(sketch, "E31.7.1.0", {"start": v(64.26, 102.9) * mm, "end": v(73.24, 111.89) * mm});
            skLineSegment(sketch, "E31.7.1.1", {"start": v(73.24, 93.93) * mm, "end": v(64.26, 102.9) * mm});
            skLineSegment(sketch, "E31.7.1.2", {"start": v(82.22, 102.9) * mm, "end": v(73.24, 93.93) * mm});
            skLineSegment(sketch, "E31.7.1.3", {"start": v(73.24, 111.89) * mm, "end": v(82.22, 102.9) * mm});
            skLineSegment(sketch, "E31.7.2.0", {"start": v(64.26, 78.01) * mm, "end": v(73.24, 87) * mm});
            skLineSegment(sketch, "E31.7.2.1", {"start": v(73.24, 69.03) * mm, "end": v(64.26, 78.01) * mm});
            skLineSegment(sketch, "E31.7.2.2", {"start": v(82.22, 78.01) * mm, "end": v(73.24, 69.03) * mm});
            skLineSegment(sketch, "E31.7.2.3", {"start": v(73.24, 87) * mm, "end": v(82.22, 78.01) * mm});
            skLineSegment(sketch, "E31.7.3.0", {"start": v(64.26, 53.12) * mm, "end": v(73.24, 62.1) * mm});
            skLineSegment(sketch, "E31.7.3.1", {"start": v(73.24, 44.14) * mm, "end": v(64.26, 53.12) * mm});
            skLineSegment(sketch, "E31.7.3.2", {"start": v(82.22, 53.12) * mm, "end": v(73.24, 44.14) * mm});
            skLineSegment(sketch, "E31.7.3.3", {"start": v(73.24, 62.1) * mm, "end": v(82.22, 53.12) * mm});
            skLineSegment(sketch, "E31.7.4.0", {"start": v(64.26, 28.23) * mm, "end": v(73.24, 37.21) * mm});
            skLineSegment(sketch, "E31.7.4.1", {"start": v(73.24, 19.25) * mm, "end": v(64.26, 28.23) * mm});
            skLineSegment(sketch, "E31.7.4.2", {"start": v(82.22, 28.23) * mm, "end": v(73.24, 19.25) * mm});
            skLineSegment(sketch, "E31.7.4.3", {"start": v(73.24, 37.21) * mm, "end": v(82.22, 28.23) * mm});
            skLineSegment(sketch, "E31.8.0.0", {"start": v(88.9, 127.8) * mm, "end": v(97.88, 136.78) * mm});
            skLineSegment(sketch, "E31.8.0.1", {"start": v(97.88, 118.82) * mm, "end": v(88.9, 127.8) * mm});
            skLineSegment(sketch, "E31.8.0.2", {"start": v(106.86, 127.8) * mm, "end": v(97.88, 118.82) * mm});
            skLineSegment(sketch, "E31.8.0.3", {"start": v(97.88, 136.78) * mm, "end": v(106.86, 127.8) * mm});
            skLineSegment(sketch, "E31.8.1.0", {"start": v(88.9, 102.9) * mm, "end": v(97.88, 111.89) * mm});
            skLineSegment(sketch, "E31.8.1.1", {"start": v(97.88, 93.93) * mm, "end": v(88.9, 102.9) * mm});
            skLineSegment(sketch, "E31.8.1.2", {"start": v(106.86, 102.9) * mm, "end": v(97.88, 93.93) * mm});
            skLineSegment(sketch, "E31.8.1.3", {"start": v(97.88, 111.89) * mm, "end": v(106.86, 102.9) * mm});
            skLineSegment(sketch, "E31.8.2.0", {"start": v(88.9, 78.01) * mm, "end": v(97.88, 87) * mm});
            skLineSegment(sketch, "E31.8.2.1", {"start": v(97.88, 69.03) * mm, "end": v(88.9, 78.01) * mm});
            skLineSegment(sketch, "E31.8.2.2", {"start": v(106.86, 78.01) * mm, "end": v(97.88, 69.03) * mm});
            skLineSegment(sketch, "E31.8.2.3", {"start": v(97.88, 87) * mm, "end": v(106.86, 78.01) * mm});
            skLineSegment(sketch, "E31.8.3.0", {"start": v(88.9, 53.12) * mm, "end": v(97.88, 62.1) * mm});
            skLineSegment(sketch, "E31.8.3.1", {"start": v(97.88, 44.14) * mm, "end": v(88.9, 53.12) * mm});
            skLineSegment(sketch, "E31.8.3.2", {"start": v(106.86, 53.12) * mm, "end": v(97.88, 44.14) * mm});
            skLineSegment(sketch, "E31.8.3.3", {"start": v(97.88, 62.1) * mm, "end": v(106.86, 53.12) * mm});
            skLineSegment(sketch, "E31.8.4.0", {"start": v(88.9, 28.23) * mm, "end": v(97.88, 37.21) * mm});
            skLineSegment(sketch, "E31.8.4.1", {"start": v(97.88, 19.25) * mm, "end": v(88.9, 28.23) * mm});
            skLineSegment(sketch, "E31.8.4.2", {"start": v(106.86, 28.23) * mm, "end": v(97.88, 19.25) * mm});
            skLineSegment(sketch, "E31.8.4.3", {"start": v(97.88, 37.21) * mm, "end": v(106.86, 28.23) * mm});
            skLineSegment(sketch, "E31.direction1", {"start": v(-108.2, 127.8) * mm, "end": v(-83.57, 127.8) * mm, "construction": true});
            skLineSegment(sketch, "E31.direction2", {"start": v(-108.2, 127.8) * mm, "end": v(-108.2, 102.9) * mm, "construction": true});
            skSolve(sketch);
        }
        {
            var Q0;
            Q0 = qSketchRegion(id + "F12", true);
            extrude(context, id + "F13", {"entities" : qUnion([Q0]), "operationType" : NewBodyOperationType.REMOVE, "endBound" : BoundingType.THROUGH_ALL, "oppositeDirection" : true, "depth" : 25.4 * mm});
        }
        {
            var Q0;
            Q0=makeQuery(id+"F3.boolean.opBoolean","MERGE",FACE,{"derivedFrom":[makeQuery(id+"F1.opExtrude","SWEPT_FACE",FACE,{"disambiguationData":[OSD([sQuery(id+"F0.wireOp",EDGE,"E0.top")])]}),makeQuery(id+"F3.opExtrude","SWEPT_FACE",FACE,{"disambiguationData":[OSD([sQuery(id+"F2.wireOp",EDGE,"E1.top")])]})]});
            var sketch = newSketch(context, id + "F14", { "sketchPlane" : qUnion([Q0])});
            skLineSegment(sketch, "E32", {"start": v(-101.6, 155.58) * mm, "end": v(-63.5, 88.9) * mm});
            skLineSegment(sketch, "E33", {"start": v(-63.5, 88.9) * mm, "end": v(63.5, 88.9) * mm});
            skLineSegment(sketch, "E34", {"start": v(63.5, 88.9) * mm, "end": v(101.6, 155.58) * mm});
            skLineSegment(sketch, "E35.0", {"start": v(67.19, 82.55) * mm, "end": v(107.11, 152.42) * mm});
            skLineSegment(sketch, "E35.1", {"start": v(-67.19, 82.55) * mm, "end": v(67.19, 82.55) * mm});
            skLineSegment(sketch, "E35.2", {"start": v(-107.11, 152.42) * mm, "end": v(-67.19, 82.55) * mm});
            skLineSegment(sketch, "E36", {"start": v(-107.11, 152.42) * mm, "end": v(-107.11, 155.58) * mm});
            skLineSegment(sketch, "E37", {"start": v(-107.11, 155.58) * mm, "end": v(-101.6, 155.58) * mm});
            skLineSegment(sketch, "E38", {"start": v(107.11, 152.42) * mm, "end": v(107.11, 155.58) * mm});
            skLineSegment(sketch, "E39", {"start": v(107.11, 155.58) * mm, "end": v(101.6, 155.58) * mm});
            skSolve(sketch);
        }
        {
            var Q0;
            Q0 = qSketchRegion(id + "F14", true);
            extrude(context, id + "F15", {"entities" : qUnion([Q0]), "operationType" : NewBodyOperationType.ADD, "oppositeDirection" : true, "depth" : 3.17 * mm});
        }
        {
            var Q0;
            Q0=makeQuery(id+"F1.opExtrude","CAP_FACE",FACE,{"disambiguationData":[OSD([sQuery(id+"F0.wireOp",EDGE,"E0.bottom"),sQuery(id+"F0.wireOp",EDGE,"E0.top"),sQuery(id+"F0.wireOp",EDGE,"E0.left"),sQuery(id+"F0.wireOp",EDGE,"E0.right")])],"isStart":false});
            var sketch = newSketch(context, id + "F16", { "sketchPlane" : qUnion([Q0])});
            skLineSegment(sketch, "E40.bottom", {"start": v(-98.42, 98.42) * mm, "end": v(-117.47, 98.42) * mm});
            skLineSegment(sketch, "E40.top", {"start": v(-98.42, 117.47) * mm, "end": v(-117.47, 117.47) * mm});
            skLineSegment(sketch, "E40.left", {"start": v(-98.42, 98.42) * mm, "end": v(-98.42, 117.47) * mm});
            skLineSegment(sketch, "E40.right", {"start": v(-117.47, 98.42) * mm, "end": v(-117.47, 117.47) * mm});
            skPoint(sketch, "E40.middle", {"position": v(-107.95, 107.95) * mm});
            skLineSegment(sketch, "E41.0.1.0", {"start": v(-98.42, 71.5) * mm, "end": v(-117.47, 71.5) * mm});
            skLineSegment(sketch, "E41.0.1.1", {"start": v(-117.47, 71.5) * mm, "end": v(-117.47, 90.55) * mm});
            skLineSegment(sketch, "E41.0.1.2", {"start": v(-98.42, 90.55) * mm, "end": v(-117.47, 90.55) * mm});
            skLineSegment(sketch, "E41.0.1.3", {"start": v(-98.42, 71.5) * mm, "end": v(-98.42, 90.55) * mm});
            skLineSegment(sketch, "E41.0.2.0", {"start": v(-98.42, 44.58) * mm, "end": v(-117.47, 44.58) * mm});
            skLineSegment(sketch, "E41.0.2.1", {"start": v(-117.47, 44.58) * mm, "end": v(-117.47, 63.63) * mm});
            skLineSegment(sketch, "E41.0.2.2", {"start": v(-98.42, 63.63) * mm, "end": v(-117.47, 63.63) * mm});
            skLineSegment(sketch, "E41.0.2.3", {"start": v(-98.42, 44.58) * mm, "end": v(-98.42, 63.63) * mm});
            skLineSegment(sketch, "E41.0.3.0", {"start": v(-98.42, 17.65) * mm, "end": v(-117.47, 17.65) * mm});
            skLineSegment(sketch, "E41.0.3.1", {"start": v(-117.47, 17.65) * mm, "end": v(-117.47, 36.7) * mm});
            skLineSegment(sketch, "E41.0.3.2", {"start": v(-98.42, 36.7) * mm, "end": v(-117.47, 36.7) * mm});
            skLineSegment(sketch, "E41.0.3.3", {"start": v(-98.42, 17.65) * mm, "end": v(-98.42, 36.7) * mm});
            skLineSegment(sketch, "E41.0.4.0", {"start": v(-98.42, -9.27) * mm, "end": v(-117.47, -9.27) * mm});
            skLineSegment(sketch, "E41.0.4.1", {"start": v(-117.47, -9.27) * mm, "end": v(-117.47, 9.78) * mm});
            skLineSegment(sketch, "E41.0.4.2", {"start": v(-98.42, 9.78) * mm, "end": v(-117.47, 9.78) * mm});
            skLineSegment(sketch, "E41.0.4.3", {"start": v(-98.42, -9.27) * mm, "end": v(-98.42, 9.78) * mm});
            skLineSegment(sketch, "E41.0.5.0", {"start": v(-98.42, -36.2) * mm, "end": v(-117.47, -36.2) * mm});
            skLineSegment(sketch, "E41.0.5.1", {"start": v(-117.47, -36.2) * mm, "end": v(-117.47, -17.15) * mm});
            skLineSegment(sketch, "E41.0.5.2", {"start": v(-98.42, -17.15) * mm, "end": v(-117.47, -17.15) * mm});
            skLineSegment(sketch, "E41.0.5.3", {"start": v(-98.42, -36.2) * mm, "end": v(-98.42, -17.15) * mm});
            skLineSegment(sketch, "E41.0.6.0", {"start": v(-98.42, -63.12) * mm, "end": v(-117.47, -63.12) * mm});
            skLineSegment(sketch, "E41.0.6.1", {"start": v(-117.47, -63.12) * mm, "end": v(-117.47, -44.07) * mm});
            skLineSegment(sketch, "E41.0.6.2", {"start": v(-98.42, -44.07) * mm, "end": v(-117.47, -44.07) * mm});
            skLineSegment(sketch, "E41.0.6.3", {"start": v(-98.42, -63.12) * mm, "end": v(-98.42, -44.07) * mm});
            skLineSegment(sketch, "E41.0.7.0", {"start": v(-98.42, -90.04) * mm, "end": v(-117.47, -90.04) * mm});
            skLineSegment(sketch, "E41.0.7.1", {"start": v(-117.47, -90.04) * mm, "end": v(-117.47, -71) * mm});
            skLineSegment(sketch, "E41.0.7.2", {"start": v(-98.42, -71) * mm, "end": v(-117.47, -71) * mm});
            skLineSegment(sketch, "E41.0.7.3", {"start": v(-98.42, -90.04) * mm, "end": v(-98.42, -71) * mm});
            skLineSegment(sketch, "E41.0.8.0", {"start": v(-98.42, -116.97) * mm, "end": v(-117.47, -116.97) * mm});
            skLineSegment(sketch, "E41.0.8.1", {"start": v(-117.47, -116.97) * mm, "end": v(-117.47, -97.92) * mm});
            skLineSegment(sketch, "E41.0.8.2", {"start": v(-98.42, -97.92) * mm, "end": v(-117.47, -97.92) * mm});
            skLineSegment(sketch, "E41.0.8.3", {"start": v(-98.42, -116.97) * mm, "end": v(-98.42, -97.92) * mm});
            skLineSegment(sketch, "E41.1.0.0", {"start": v(-71.5, 98.42) * mm, "end": v(-90.55, 98.42) * mm});
            skLineSegment(sketch, "E41.1.0.1", {"start": v(-90.55, 98.42) * mm, "end": v(-90.55, 117.47) * mm});
            skLineSegment(sketch, "E41.1.0.2", {"start": v(-71.5, 117.47) * mm, "end": v(-90.55, 117.47) * mm});
            skLineSegment(sketch, "E41.1.0.3", {"start": v(-71.5, 98.42) * mm, "end": v(-71.5, 117.47) * mm});
            skLineSegment(sketch, "E41.1.1.0", {"start": v(-71.5, 71.5) * mm, "end": v(-90.55, 71.5) * mm});
            skLineSegment(sketch, "E41.1.1.1", {"start": v(-90.55, 71.5) * mm, "end": v(-90.55, 90.55) * mm});
            skLineSegment(sketch, "E41.1.1.2", {"start": v(-71.5, 90.55) * mm, "end": v(-90.55, 90.55) * mm});
            skLineSegment(sketch, "E41.1.1.3", {"start": v(-71.5, 71.5) * mm, "end": v(-71.5, 90.55) * mm});
            skLineSegment(sketch, "E41.1.2.0", {"start": v(-71.5, 44.58) * mm, "end": v(-90.55, 44.58) * mm});
            skLineSegment(sketch, "E41.1.2.1", {"start": v(-90.55, 44.58) * mm, "end": v(-90.55, 63.63) * mm});
            skLineSegment(sketch, "E41.1.2.2", {"start": v(-71.5, 63.63) * mm, "end": v(-90.55, 63.63) * mm});
            skLineSegment(sketch, "E41.1.2.3", {"start": v(-71.5, 44.58) * mm, "end": v(-71.5, 63.63) * mm});
            skLineSegment(sketch, "E41.1.3.0", {"start": v(-71.5, 17.65) * mm, "end": v(-90.55, 17.65) * mm});
            skLineSegment(sketch, "E41.1.3.1", {"start": v(-90.55, 17.65) * mm, "end": v(-90.55, 36.7) * mm});
            skLineSegment(sketch, "E41.1.3.2", {"start": v(-71.5, 36.7) * mm, "end": v(-90.55, 36.7) * mm});
            skLineSegment(sketch, "E41.1.3.3", {"start": v(-71.5, 17.65) * mm, "end": v(-71.5, 36.7) * mm});
            skLineSegment(sketch, "E41.1.4.0", {"start": v(-71.5, -9.27) * mm, "end": v(-90.55, -9.27) * mm});
            skLineSegment(sketch, "E41.1.4.1", {"start": v(-90.55, -9.27) * mm, "end": v(-90.55, 9.78) * mm});
            skLineSegment(sketch, "E41.1.4.2", {"start": v(-71.5, 9.78) * mm, "end": v(-90.55, 9.78) * mm});
            skLineSegment(sketch, "E41.1.4.3", {"start": v(-71.5, -9.27) * mm, "end": v(-71.5, 9.78) * mm});
            skLineSegment(sketch, "E41.1.5.0", {"start": v(-71.5, -36.2) * mm, "end": v(-90.55, -36.2) * mm});
            skLineSegment(sketch, "E41.1.5.1", {"start": v(-90.55, -36.2) * mm, "end": v(-90.55, -17.15) * mm});
            skLineSegment(sketch, "E41.1.5.2", {"start": v(-71.5, -17.15) * mm, "end": v(-90.55, -17.15) * mm});
            skLineSegment(sketch, "E41.1.5.3", {"start": v(-71.5, -36.2) * mm, "end": v(-71.5, -17.15) * mm});
            skLineSegment(sketch, "E41.1.6.0", {"start": v(-71.5, -63.12) * mm, "end": v(-90.55, -63.12) * mm});
            skLineSegment(sketch, "E41.1.6.1", {"start": v(-90.55, -63.12) * mm, "end": v(-90.55, -44.07) * mm});
            skLineSegment(sketch, "E41.1.6.2", {"start": v(-71.5, -44.07) * mm, "end": v(-90.55, -44.07) * mm});
            skLineSegment(sketch, "E41.1.6.3", {"start": v(-71.5, -63.12) * mm, "end": v(-71.5, -44.07) * mm});
            skLineSegment(sketch, "E41.1.7.0", {"start": v(-71.5, -90.04) * mm, "end": v(-90.55, -90.04) * mm});
            skLineSegment(sketch, "E41.1.7.1", {"start": v(-90.55, -90.04) * mm, "end": v(-90.55, -71) * mm});
            skLineSegment(sketch, "E41.1.7.2", {"start": v(-71.5, -71) * mm, "end": v(-90.55, -71) * mm});
            skLineSegment(sketch, "E41.1.7.3", {"start": v(-71.5, -90.04) * mm, "end": v(-71.5, -71) * mm});
            skLineSegment(sketch, "E41.1.8.0", {"start": v(-71.5, -116.97) * mm, "end": v(-90.55, -116.97) * mm});
            skLineSegment(sketch, "E41.1.8.1", {"start": v(-90.55, -116.97) * mm, "end": v(-90.55, -97.92) * mm});
            skLineSegment(sketch, "E41.1.8.2", {"start": v(-71.5, -97.92) * mm, "end": v(-90.55, -97.92) * mm});
            skLineSegment(sketch, "E41.1.8.3", {"start": v(-71.5, -116.97) * mm, "end": v(-71.5, -97.92) * mm});
            skLineSegment(sketch, "E41.2.0.0", {"start": v(-44.58, 98.42) * mm, "end": v(-63.63, 98.42) * mm});
            skLineSegment(sketch, "E41.2.0.1", {"start": v(-63.63, 98.42) * mm, "end": v(-63.63, 117.47) * mm});
            skLineSegment(sketch, "E41.2.0.2", {"start": v(-44.58, 117.47) * mm, "end": v(-63.63, 117.47) * mm});
            skLineSegment(sketch, "E41.2.0.3", {"start": v(-44.58, 98.42) * mm, "end": v(-44.58, 117.47) * mm});
            skLineSegment(sketch, "E41.2.1.0", {"start": v(-44.58, 71.5) * mm, "end": v(-63.63, 71.5) * mm});
            skLineSegment(sketch, "E41.2.1.1", {"start": v(-63.63, 71.5) * mm, "end": v(-63.63, 90.55) * mm});
            skLineSegment(sketch, "E41.2.1.2", {"start": v(-44.58, 90.55) * mm, "end": v(-63.63, 90.55) * mm});
            skLineSegment(sketch, "E41.2.1.3", {"start": v(-44.58, 71.5) * mm, "end": v(-44.58, 90.55) * mm});
            skLineSegment(sketch, "E41.2.2.0", {"start": v(-44.58, 44.58) * mm, "end": v(-63.63, 44.58) * mm});
            skLineSegment(sketch, "E41.2.2.1", {"start": v(-63.63, 44.58) * mm, "end": v(-63.63, 63.63) * mm});
            skLineSegment(sketch, "E41.2.2.2", {"start": v(-44.58, 63.63) * mm, "end": v(-63.63, 63.63) * mm});
            skLineSegment(sketch, "E41.2.2.3", {"start": v(-44.58, 44.58) * mm, "end": v(-44.58, 63.63) * mm});
            skLineSegment(sketch, "E41.2.3.0", {"start": v(-44.58, 17.65) * mm, "end": v(-63.63, 17.65) * mm});
            skLineSegment(sketch, "E41.2.3.1", {"start": v(-63.63, 17.65) * mm, "end": v(-63.63, 36.7) * mm});
            skLineSegment(sketch, "E41.2.3.2", {"start": v(-44.58, 36.7) * mm, "end": v(-63.63, 36.7) * mm});
            skLineSegment(sketch, "E41.2.3.3", {"start": v(-44.58, 17.65) * mm, "end": v(-44.58, 36.7) * mm});
            skLineSegment(sketch, "E41.2.4.0", {"start": v(-44.58, -9.27) * mm, "end": v(-63.63, -9.27) * mm});
            skLineSegment(sketch, "E41.2.4.1", {"start": v(-63.63, -9.27) * mm, "end": v(-63.63, 9.78) * mm});
            skLineSegment(sketch, "E41.2.4.2", {"start": v(-44.58, 9.78) * mm, "end": v(-63.63, 9.78) * mm});
            skLineSegment(sketch, "E41.2.4.3", {"start": v(-44.58, -9.27) * mm, "end": v(-44.58, 9.78) * mm});
            skLineSegment(sketch, "E41.2.5.0", {"start": v(-44.58, -36.2) * mm, "end": v(-63.63, -36.2) * mm});
            skLineSegment(sketch, "E41.2.5.1", {"start": v(-63.63, -36.2) * mm, "end": v(-63.63, -17.15) * mm});
            skLineSegment(sketch, "E41.2.5.2", {"start": v(-44.58, -17.15) * mm, "end": v(-63.63, -17.15) * mm});
            skLineSegment(sketch, "E41.2.5.3", {"start": v(-44.58, -36.2) * mm, "end": v(-44.58, -17.15) * mm});
            skLineSegment(sketch, "E41.2.6.0", {"start": v(-44.58, -63.12) * mm, "end": v(-63.63, -63.12) * mm});
            skLineSegment(sketch, "E41.2.6.1", {"start": v(-63.63, -63.12) * mm, "end": v(-63.63, -44.07) * mm});
            skLineSegment(sketch, "E41.2.6.2", {"start": v(-44.58, -44.07) * mm, "end": v(-63.63, -44.07) * mm});
            skLineSegment(sketch, "E41.2.6.3", {"start": v(-44.58, -63.12) * mm, "end": v(-44.58, -44.07) * mm});
            skLineSegment(sketch, "E41.2.7.0", {"start": v(-44.58, -90.04) * mm, "end": v(-63.63, -90.04) * mm});
            skLineSegment(sketch, "E41.2.7.1", {"start": v(-63.63, -90.04) * mm, "end": v(-63.63, -71) * mm});
            skLineSegment(sketch, "E41.2.7.2", {"start": v(-44.58, -71) * mm, "end": v(-63.63, -71) * mm});
            skLineSegment(sketch, "E41.2.7.3", {"start": v(-44.58, -90.04) * mm, "end": v(-44.58, -71) * mm});
            skLineSegment(sketch, "E41.2.8.0", {"start": v(-44.58, -116.97) * mm, "end": v(-63.63, -116.97) * mm});
            skLineSegment(sketch, "E41.2.8.1", {"start": v(-63.63, -116.97) * mm, "end": v(-63.63, -97.92) * mm});
            skLineSegment(sketch, "E41.2.8.2", {"start": v(-44.58, -97.92) * mm, "end": v(-63.63, -97.92) * mm});
            skLineSegment(sketch, "E41.2.8.3", {"start": v(-44.58, -116.97) * mm, "end": v(-44.58, -97.92) * mm});
            skLineSegment(sketch, "E41.3.0.0", {"start": v(-17.65, 98.42) * mm, "end": v(-36.7, 98.42) * mm});
            skLineSegment(sketch, "E41.3.0.1", {"start": v(-36.7, 98.42) * mm, "end": v(-36.7, 117.47) * mm});
            skLineSegment(sketch, "E41.3.0.2", {"start": v(-17.65, 117.47) * mm, "end": v(-36.7, 117.47) * mm});
            skLineSegment(sketch, "E41.3.0.3", {"start": v(-17.65, 98.42) * mm, "end": v(-17.65, 117.47) * mm});
            skLineSegment(sketch, "E41.3.1.0", {"start": v(-17.65, 71.5) * mm, "end": v(-36.7, 71.5) * mm});
            skLineSegment(sketch, "E41.3.1.1", {"start": v(-36.7, 71.5) * mm, "end": v(-36.7, 90.55) * mm});
            skLineSegment(sketch, "E41.3.1.2", {"start": v(-17.65, 90.55) * mm, "end": v(-36.7, 90.55) * mm});
            skLineSegment(sketch, "E41.3.1.3", {"start": v(-17.65, 71.5) * mm, "end": v(-17.65, 90.55) * mm});
            skLineSegment(sketch, "E41.3.2.0", {"start": v(-17.65, 44.58) * mm, "end": v(-36.7, 44.58) * mm});
            skLineSegment(sketch, "E41.3.2.1", {"start": v(-36.7, 44.58) * mm, "end": v(-36.7, 63.63) * mm});
            skLineSegment(sketch, "E41.3.2.2", {"start": v(-17.65, 63.63) * mm, "end": v(-36.7, 63.63) * mm});
            skLineSegment(sketch, "E41.3.2.3", {"start": v(-17.65, 44.58) * mm, "end": v(-17.65, 63.63) * mm});
            skLineSegment(sketch, "E41.3.3.0", {"start": v(-17.65, 17.65) * mm, "end": v(-36.7, 17.65) * mm});
            skLineSegment(sketch, "E41.3.3.1", {"start": v(-36.7, 17.65) * mm, "end": v(-36.7, 36.7) * mm});
            skLineSegment(sketch, "E41.3.3.2", {"start": v(-17.65, 36.7) * mm, "end": v(-36.7, 36.7) * mm});
            skLineSegment(sketch, "E41.3.3.3", {"start": v(-17.65, 17.65) * mm, "end": v(-17.65, 36.7) * mm});
            skLineSegment(sketch, "E41.3.4.0", {"start": v(-17.65, -9.27) * mm, "end": v(-36.7, -9.27) * mm});
            skLineSegment(sketch, "E41.3.4.1", {"start": v(-36.7, -9.27) * mm, "end": v(-36.7, 9.78) * mm});
            skLineSegment(sketch, "E41.3.4.2", {"start": v(-17.65, 9.78) * mm, "end": v(-36.7, 9.78) * mm});
            skLineSegment(sketch, "E41.3.4.3", {"start": v(-17.65, -9.27) * mm, "end": v(-17.65, 9.78) * mm});
            skLineSegment(sketch, "E41.3.5.0", {"start": v(-17.65, -36.2) * mm, "end": v(-36.7, -36.2) * mm});
            skLineSegment(sketch, "E41.3.5.1", {"start": v(-36.7, -36.2) * mm, "end": v(-36.7, -17.15) * mm});
            skLineSegment(sketch, "E41.3.5.2", {"start": v(-17.65, -17.15) * mm, "end": v(-36.7, -17.15) * mm});
            skLineSegment(sketch, "E41.3.5.3", {"start": v(-17.65, -36.2) * mm, "end": v(-17.65, -17.15) * mm});
            skLineSegment(sketch, "E41.3.6.0", {"start": v(-17.65, -63.12) * mm, "end": v(-36.7, -63.12) * mm});
            skLineSegment(sketch, "E41.3.6.1", {"start": v(-36.7, -63.12) * mm, "end": v(-36.7, -44.07) * mm});
            skLineSegment(sketch, "E41.3.6.2", {"start": v(-17.65, -44.07) * mm, "end": v(-36.7, -44.07) * mm});
            skLineSegment(sketch, "E41.3.6.3", {"start": v(-17.65, -63.12) * mm, "end": v(-17.65, -44.07) * mm});
            skLineSegment(sketch, "E41.3.7.0", {"start": v(-17.65, -90.04) * mm, "end": v(-36.7, -90.04) * mm});
            skLineSegment(sketch, "E41.3.7.1", {"start": v(-36.7, -90.04) * mm, "end": v(-36.7, -71) * mm});
            skLineSegment(sketch, "E41.3.7.2", {"start": v(-17.65, -71) * mm, "end": v(-36.7, -71) * mm});
            skLineSegment(sketch, "E41.3.7.3", {"start": v(-17.65, -90.04) * mm, "end": v(-17.65, -71) * mm});
            skLineSegment(sketch, "E41.3.8.0", {"start": v(-17.65, -116.97) * mm, "end": v(-36.7, -116.97) * mm});
            skLineSegment(sketch, "E41.3.8.1", {"start": v(-36.7, -116.97) * mm, "end": v(-36.7, -97.92) * mm});
            skLineSegment(sketch, "E41.3.8.2", {"start": v(-17.65, -97.92) * mm, "end": v(-36.7, -97.92) * mm});
            skLineSegment(sketch, "E41.3.8.3", {"start": v(-17.65, -116.97) * mm, "end": v(-17.65, -97.92) * mm});
            skLineSegment(sketch, "E41.4.0.0", {"start": v(9.27, 98.42) * mm, "end": v(-9.78, 98.42) * mm});
            skLineSegment(sketch, "E41.4.0.1", {"start": v(-9.78, 98.42) * mm, "end": v(-9.78, 117.47) * mm});
            skLineSegment(sketch, "E41.4.0.2", {"start": v(9.27, 117.47) * mm, "end": v(-9.78, 117.47) * mm});
            skLineSegment(sketch, "E41.4.0.3", {"start": v(9.27, 98.42) * mm, "end": v(9.27, 117.47) * mm});
            skLineSegment(sketch, "E41.4.1.0", {"start": v(9.27, 71.5) * mm, "end": v(-9.78, 71.5) * mm});
            skLineSegment(sketch, "E41.4.1.1", {"start": v(-9.78, 71.5) * mm, "end": v(-9.78, 90.55) * mm});
            skLineSegment(sketch, "E41.4.1.2", {"start": v(9.27, 90.55) * mm, "end": v(-9.78, 90.55) * mm});
            skLineSegment(sketch, "E41.4.1.3", {"start": v(9.27, 71.5) * mm, "end": v(9.27, 90.55) * mm});
            skLineSegment(sketch, "E41.4.2.0", {"start": v(9.27, 44.58) * mm, "end": v(-9.78, 44.58) * mm});
            skLineSegment(sketch, "E41.4.2.1", {"start": v(-9.78, 44.58) * mm, "end": v(-9.78, 63.63) * mm});
            skLineSegment(sketch, "E41.4.2.2", {"start": v(9.27, 63.63) * mm, "end": v(-9.78, 63.63) * mm});
            skLineSegment(sketch, "E41.4.2.3", {"start": v(9.27, 44.58) * mm, "end": v(9.27, 63.63) * mm});
            skLineSegment(sketch, "E41.4.3.0", {"start": v(9.27, 17.65) * mm, "end": v(-9.78, 17.65) * mm});
            skLineSegment(sketch, "E41.4.3.1", {"start": v(-9.78, 17.65) * mm, "end": v(-9.78, 36.7) * mm});
            skLineSegment(sketch, "E41.4.3.2", {"start": v(9.27, 36.7) * mm, "end": v(-9.78, 36.7) * mm});
            skLineSegment(sketch, "E41.4.3.3", {"start": v(9.27, 17.65) * mm, "end": v(9.27, 36.7) * mm});
            skLineSegment(sketch, "E41.4.4.0", {"start": v(9.27, -9.27) * mm, "end": v(-9.78, -9.27) * mm});
            skLineSegment(sketch, "E41.4.4.1", {"start": v(-9.78, -9.27) * mm, "end": v(-9.78, 9.78) * mm});
            skLineSegment(sketch, "E41.4.4.2", {"start": v(9.27, 9.78) * mm, "end": v(-9.78, 9.78) * mm});
            skLineSegment(sketch, "E41.4.4.3", {"start": v(9.27, -9.27) * mm, "end": v(9.27, 9.78) * mm});
            skLineSegment(sketch, "E41.4.5.0", {"start": v(9.27, -36.2) * mm, "end": v(-9.78, -36.2) * mm});
            skLineSegment(sketch, "E41.4.5.1", {"start": v(-9.78, -36.2) * mm, "end": v(-9.78, -17.15) * mm});
            skLineSegment(sketch, "E41.4.5.2", {"start": v(9.27, -17.15) * mm, "end": v(-9.78, -17.15) * mm});
            skLineSegment(sketch, "E41.4.5.3", {"start": v(9.27, -36.2) * mm, "end": v(9.27, -17.15) * mm});
            skLineSegment(sketch, "E41.4.6.0", {"start": v(9.27, -63.12) * mm, "end": v(-9.78, -63.12) * mm});
            skLineSegment(sketch, "E41.4.6.1", {"start": v(-9.78, -63.12) * mm, "end": v(-9.78, -44.07) * mm});
            skLineSegment(sketch, "E41.4.6.2", {"start": v(9.27, -44.07) * mm, "end": v(-9.78, -44.07) * mm});
            skLineSegment(sketch, "E41.4.6.3", {"start": v(9.27, -63.12) * mm, "end": v(9.27, -44.07) * mm});
            skLineSegment(sketch, "E41.4.7.0", {"start": v(9.27, -90.04) * mm, "end": v(-9.78, -90.04) * mm});
            skLineSegment(sketch, "E41.4.7.1", {"start": v(-9.78, -90.04) * mm, "end": v(-9.78, -71) * mm});
            skLineSegment(sketch, "E41.4.7.2", {"start": v(9.27, -71) * mm, "end": v(-9.78, -71) * mm});
            skLineSegment(sketch, "E41.4.7.3", {"start": v(9.27, -90.04) * mm, "end": v(9.27, -71) * mm});
            skLineSegment(sketch, "E41.4.8.0", {"start": v(9.27, -116.97) * mm, "end": v(-9.78, -116.97) * mm});
            skLineSegment(sketch, "E41.4.8.1", {"start": v(-9.78, -116.97) * mm, "end": v(-9.78, -97.92) * mm});
            skLineSegment(sketch, "E41.4.8.2", {"start": v(9.27, -97.92) * mm, "end": v(-9.78, -97.92) * mm});
            skLineSegment(sketch, "E41.4.8.3", {"start": v(9.27, -116.97) * mm, "end": v(9.27, -97.92) * mm});
            skLineSegment(sketch, "E41.5.0.0", {"start": v(36.2, 98.42) * mm, "end": v(17.15, 98.42) * mm});
            skLineSegment(sketch, "E41.5.0.1", {"start": v(17.15, 98.42) * mm, "end": v(17.15, 117.47) * mm});
            skLineSegment(sketch, "E41.5.0.2", {"start": v(36.2, 117.47) * mm, "end": v(17.15, 117.47) * mm});
            skLineSegment(sketch, "E41.5.0.3", {"start": v(36.2, 98.42) * mm, "end": v(36.2, 117.47) * mm});
            skLineSegment(sketch, "E41.5.1.0", {"start": v(36.2, 71.5) * mm, "end": v(17.15, 71.5) * mm});
            skLineSegment(sketch, "E41.5.1.1", {"start": v(17.15, 71.5) * mm, "end": v(17.15, 90.55) * mm});
            skLineSegment(sketch, "E41.5.1.2", {"start": v(36.2, 90.55) * mm, "end": v(17.15, 90.55) * mm});
            skLineSegment(sketch, "E41.5.1.3", {"start": v(36.2, 71.5) * mm, "end": v(36.2, 90.55) * mm});
            skLineSegment(sketch, "E41.5.2.0", {"start": v(36.2, 44.58) * mm, "end": v(17.15, 44.58) * mm});
            skLineSegment(sketch, "E41.5.2.1", {"start": v(17.15, 44.58) * mm, "end": v(17.15, 63.63) * mm});
            skLineSegment(sketch, "E41.5.2.2", {"start": v(36.2, 63.63) * mm, "end": v(17.15, 63.63) * mm});
            skLineSegment(sketch, "E41.5.2.3", {"start": v(36.2, 44.58) * mm, "end": v(36.2, 63.63) * mm});
            skLineSegment(sketch, "E41.5.3.0", {"start": v(36.2, 17.65) * mm, "end": v(17.15, 17.65) * mm});
            skLineSegment(sketch, "E41.5.3.1", {"start": v(17.15, 17.65) * mm, "end": v(17.15, 36.7) * mm});
            skLineSegment(sketch, "E41.5.3.2", {"start": v(36.2, 36.7) * mm, "end": v(17.15, 36.7) * mm});
            skLineSegment(sketch, "E41.5.3.3", {"start": v(36.2, 17.65) * mm, "end": v(36.2, 36.7) * mm});
            skLineSegment(sketch, "E41.5.4.0", {"start": v(36.2, -9.27) * mm, "end": v(17.15, -9.27) * mm});
            skLineSegment(sketch, "E41.5.4.1", {"start": v(17.15, -9.27) * mm, "end": v(17.15, 9.78) * mm});
            skLineSegment(sketch, "E41.5.4.2", {"start": v(36.2, 9.78) * mm, "end": v(17.15, 9.78) * mm});
            skLineSegment(sketch, "E41.5.4.3", {"start": v(36.2, -9.27) * mm, "end": v(36.2, 9.78) * mm});
            skLineSegment(sketch, "E41.5.5.0", {"start": v(36.2, -36.2) * mm, "end": v(17.15, -36.2) * mm});
            skLineSegment(sketch, "E41.5.5.1", {"start": v(17.15, -36.2) * mm, "end": v(17.15, -17.15) * mm});
            skLineSegment(sketch, "E41.5.5.2", {"start": v(36.2, -17.15) * mm, "end": v(17.15, -17.15) * mm});
            skLineSegment(sketch, "E41.5.5.3", {"start": v(36.2, -36.2) * mm, "end": v(36.2, -17.15) * mm});
            skLineSegment(sketch, "E41.5.6.0", {"start": v(36.2, -63.12) * mm, "end": v(17.15, -63.12) * mm});
            skLineSegment(sketch, "E41.5.6.1", {"start": v(17.15, -63.12) * mm, "end": v(17.15, -44.07) * mm});
            skLineSegment(sketch, "E41.5.6.2", {"start": v(36.2, -44.07) * mm, "end": v(17.15, -44.07) * mm});
            skLineSegment(sketch, "E41.5.6.3", {"start": v(36.2, -63.12) * mm, "end": v(36.2, -44.07) * mm});
            skLineSegment(sketch, "E41.5.7.0", {"start": v(36.2, -90.04) * mm, "end": v(17.15, -90.04) * mm});
            skLineSegment(sketch, "E41.5.7.1", {"start": v(17.15, -90.04) * mm, "end": v(17.15, -71) * mm});
            skLineSegment(sketch, "E41.5.7.2", {"start": v(36.2, -71) * mm, "end": v(17.15, -71) * mm});
            skLineSegment(sketch, "E41.5.7.3", {"start": v(36.2, -90.04) * mm, "end": v(36.2, -71) * mm});
            skLineSegment(sketch, "E41.5.8.0", {"start": v(36.2, -116.97) * mm, "end": v(17.15, -116.97) * mm});
            skLineSegment(sketch, "E41.5.8.1", {"start": v(17.15, -116.97) * mm, "end": v(17.15, -97.92) * mm});
            skLineSegment(sketch, "E41.5.8.2", {"start": v(36.2, -97.92) * mm, "end": v(17.15, -97.92) * mm});
            skLineSegment(sketch, "E41.5.8.3", {"start": v(36.2, -116.97) * mm, "end": v(36.2, -97.92) * mm});
            skLineSegment(sketch, "E41.6.0.0", {"start": v(63.12, 98.42) * mm, "end": v(44.07, 98.42) * mm});
            skLineSegment(sketch, "E41.6.0.1", {"start": v(44.07, 98.42) * mm, "end": v(44.07, 117.47) * mm});
            skLineSegment(sketch, "E41.6.0.2", {"start": v(63.12, 117.47) * mm, "end": v(44.07, 117.47) * mm});
            skLineSegment(sketch, "E41.6.0.3", {"start": v(63.12, 98.42) * mm, "end": v(63.12, 117.47) * mm});
            skLineSegment(sketch, "E41.6.1.0", {"start": v(63.12, 71.5) * mm, "end": v(44.07, 71.5) * mm});
            skLineSegment(sketch, "E41.6.1.1", {"start": v(44.07, 71.5) * mm, "end": v(44.07, 90.55) * mm});
            skLineSegment(sketch, "E41.6.1.2", {"start": v(63.12, 90.55) * mm, "end": v(44.07, 90.55) * mm});
            skLineSegment(sketch, "E41.6.1.3", {"start": v(63.12, 71.5) * mm, "end": v(63.12, 90.55) * mm});
            skLineSegment(sketch, "E41.6.2.0", {"start": v(63.12, 44.58) * mm, "end": v(44.07, 44.58) * mm});
            skLineSegment(sketch, "E41.6.2.1", {"start": v(44.07, 44.58) * mm, "end": v(44.07, 63.63) * mm});
            skLineSegment(sketch, "E41.6.2.2", {"start": v(63.12, 63.63) * mm, "end": v(44.07, 63.63) * mm});
            skLineSegment(sketch, "E41.6.2.3", {"start": v(63.12, 44.58) * mm, "end": v(63.12, 63.63) * mm});
            skLineSegment(sketch, "E41.6.3.0", {"start": v(63.12, 17.65) * mm, "end": v(44.07, 17.65) * mm});
            skLineSegment(sketch, "E41.6.3.1", {"start": v(44.07, 17.65) * mm, "end": v(44.07, 36.7) * mm});
            skLineSegment(sketch, "E41.6.3.2", {"start": v(63.12, 36.7) * mm, "end": v(44.07, 36.7) * mm});
            skLineSegment(sketch, "E41.6.3.3", {"start": v(63.12, 17.65) * mm, "end": v(63.12, 36.7) * mm});
            skLineSegment(sketch, "E41.6.4.0", {"start": v(63.12, -9.27) * mm, "end": v(44.07, -9.27) * mm});
            skLineSegment(sketch, "E41.6.4.1", {"start": v(44.07, -9.27) * mm, "end": v(44.07, 9.78) * mm});
            skLineSegment(sketch, "E41.6.4.2", {"start": v(63.12, 9.78) * mm, "end": v(44.07, 9.78) * mm});
            skLineSegment(sketch, "E41.6.4.3", {"start": v(63.12, -9.27) * mm, "end": v(63.12, 9.78) * mm});
            skLineSegment(sketch, "E41.6.5.0", {"start": v(63.12, -36.2) * mm, "end": v(44.07, -36.2) * mm});
            skLineSegment(sketch, "E41.6.5.1", {"start": v(44.07, -36.2) * mm, "end": v(44.07, -17.15) * mm});
            skLineSegment(sketch, "E41.6.5.2", {"start": v(63.12, -17.15) * mm, "end": v(44.07, -17.15) * mm});
            skLineSegment(sketch, "E41.6.5.3", {"start": v(63.12, -36.2) * mm, "end": v(63.12, -17.15) * mm});
            skLineSegment(sketch, "E41.6.6.0", {"start": v(63.12, -63.12) * mm, "end": v(44.07, -63.12) * mm});
            skLineSegment(sketch, "E41.6.6.1", {"start": v(44.07, -63.12) * mm, "end": v(44.07, -44.07) * mm});
            skLineSegment(sketch, "E41.6.6.2", {"start": v(63.12, -44.07) * mm, "end": v(44.07, -44.07) * mm});
            skLineSegment(sketch, "E41.6.6.3", {"start": v(63.12, -63.12) * mm, "end": v(63.12, -44.07) * mm});
            skLineSegment(sketch, "E41.6.7.0", {"start": v(63.12, -90.04) * mm, "end": v(44.07, -90.04) * mm});
            skLineSegment(sketch, "E41.6.7.1", {"start": v(44.07, -90.04) * mm, "end": v(44.07, -71) * mm});
            skLineSegment(sketch, "E41.6.7.2", {"start": v(63.12, -71) * mm, "end": v(44.07, -71) * mm});
            skLineSegment(sketch, "E41.6.7.3", {"start": v(63.12, -90.04) * mm, "end": v(63.12, -71) * mm});
            skLineSegment(sketch, "E41.6.8.0", {"start": v(63.12, -116.97) * mm, "end": v(44.07, -116.97) * mm});
            skLineSegment(sketch, "E41.6.8.1", {"start": v(44.07, -116.97) * mm, "end": v(44.07, -97.92) * mm});
            skLineSegment(sketch, "E41.6.8.2", {"start": v(63.12, -97.92) * mm, "end": v(44.07, -97.92) * mm});
            skLineSegment(sketch, "E41.6.8.3", {"start": v(63.12, -116.97) * mm, "end": v(63.12, -97.92) * mm});
            skLineSegment(sketch, "E41.7.0.0", {"start": v(90.04, 98.42) * mm, "end": v(71, 98.42) * mm});
            skLineSegment(sketch, "E41.7.0.1", {"start": v(71, 98.42) * mm, "end": v(71, 117.47) * mm});
            skLineSegment(sketch, "E41.7.0.2", {"start": v(90.04, 117.47) * mm, "end": v(71, 117.47) * mm});
            skLineSegment(sketch, "E41.7.0.3", {"start": v(90.04, 98.42) * mm, "end": v(90.04, 117.47) * mm});
            skLineSegment(sketch, "E41.7.1.0", {"start": v(90.04, 71.5) * mm, "end": v(71, 71.5) * mm});
            skLineSegment(sketch, "E41.7.1.1", {"start": v(71, 71.5) * mm, "end": v(71, 90.55) * mm});
            skLineSegment(sketch, "E41.7.1.2", {"start": v(90.04, 90.55) * mm, "end": v(71, 90.55) * mm});
            skLineSegment(sketch, "E41.7.1.3", {"start": v(90.04, 71.5) * mm, "end": v(90.04, 90.55) * mm});
            skLineSegment(sketch, "E41.7.2.0", {"start": v(90.04, 44.58) * mm, "end": v(71, 44.58) * mm});
            skLineSegment(sketch, "E41.7.2.1", {"start": v(71, 44.58) * mm, "end": v(71, 63.63) * mm});
            skLineSegment(sketch, "E41.7.2.2", {"start": v(90.04, 63.63) * mm, "end": v(71, 63.63) * mm});
            skLineSegment(sketch, "E41.7.2.3", {"start": v(90.04, 44.58) * mm, "end": v(90.04, 63.63) * mm});
            skLineSegment(sketch, "E41.7.3.0", {"start": v(90.04, 17.65) * mm, "end": v(71, 17.65) * mm});
            skLineSegment(sketch, "E41.7.3.1", {"start": v(71, 17.65) * mm, "end": v(71, 36.7) * mm});
            skLineSegment(sketch, "E41.7.3.2", {"start": v(90.04, 36.7) * mm, "end": v(71, 36.7) * mm});
            skLineSegment(sketch, "E41.7.3.3", {"start": v(90.04, 17.65) * mm, "end": v(90.04, 36.7) * mm});
            skLineSegment(sketch, "E41.7.4.0", {"start": v(90.04, -9.27) * mm, "end": v(71, -9.27) * mm});
            skLineSegment(sketch, "E41.7.4.1", {"start": v(71, -9.27) * mm, "end": v(71, 9.78) * mm});
            skLineSegment(sketch, "E41.7.4.2", {"start": v(90.04, 9.78) * mm, "end": v(71, 9.78) * mm});
            skLineSegment(sketch, "E41.7.4.3", {"start": v(90.04, -9.27) * mm, "end": v(90.04, 9.78) * mm});
            skLineSegment(sketch, "E41.7.5.0", {"start": v(90.04, -36.2) * mm, "end": v(71, -36.2) * mm});
            skLineSegment(sketch, "E41.7.5.1", {"start": v(71, -36.2) * mm, "end": v(71, -17.15) * mm});
            skLineSegment(sketch, "E41.7.5.2", {"start": v(90.04, -17.15) * mm, "end": v(71, -17.15) * mm});
            skLineSegment(sketch, "E41.7.5.3", {"start": v(90.04, -36.2) * mm, "end": v(90.04, -17.15) * mm});
            skLineSegment(sketch, "E41.7.6.0", {"start": v(90.04, -63.12) * mm, "end": v(71, -63.12) * mm});
            skLineSegment(sketch, "E41.7.6.1", {"start": v(71, -63.12) * mm, "end": v(71, -44.07) * mm});
            skLineSegment(sketch, "E41.7.6.2", {"start": v(90.04, -44.07) * mm, "end": v(71, -44.07) * mm});
            skLineSegment(sketch, "E41.7.6.3", {"start": v(90.04, -63.12) * mm, "end": v(90.04, -44.07) * mm});
            skLineSegment(sketch, "E41.7.7.0", {"start": v(90.04, -90.04) * mm, "end": v(71, -90.04) * mm});
            skLineSegment(sketch, "E41.7.7.1", {"start": v(71, -90.04) * mm, "end": v(71, -71) * mm});
            skLineSegment(sketch, "E41.7.7.2", {"start": v(90.04, -71) * mm, "end": v(71, -71) * mm});
            skLineSegment(sketch, "E41.7.7.3", {"start": v(90.04, -90.04) * mm, "end": v(90.04, -71) * mm});
            skLineSegment(sketch, "E41.7.8.0", {"start": v(90.04, -116.97) * mm, "end": v(71, -116.97) * mm});
            skLineSegment(sketch, "E41.7.8.1", {"start": v(71, -116.97) * mm, "end": v(71, -97.92) * mm});
            skLineSegment(sketch, "E41.7.8.2", {"start": v(90.04, -97.92) * mm, "end": v(71, -97.92) * mm});
            skLineSegment(sketch, "E41.7.8.3", {"start": v(90.04, -116.97) * mm, "end": v(90.04, -97.92) * mm});
            skLineSegment(sketch, "E41.8.0.0", {"start": v(116.97, 98.42) * mm, "end": v(97.92, 98.42) * mm});
            skLineSegment(sketch, "E41.8.0.1", {"start": v(97.92, 98.42) * mm, "end": v(97.92, 117.47) * mm});
            skLineSegment(sketch, "E41.8.0.2", {"start": v(116.97, 117.47) * mm, "end": v(97.92, 117.47) * mm});
            skLineSegment(sketch, "E41.8.0.3", {"start": v(116.97, 98.42) * mm, "end": v(116.97, 117.47) * mm});
            skLineSegment(sketch, "E41.8.1.0", {"start": v(116.97, 71.5) * mm, "end": v(97.92, 71.5) * mm});
            skLineSegment(sketch, "E41.8.1.1", {"start": v(97.92, 71.5) * mm, "end": v(97.92, 90.55) * mm});
            skLineSegment(sketch, "E41.8.1.2", {"start": v(116.97, 90.55) * mm, "end": v(97.92, 90.55) * mm});
            skLineSegment(sketch, "E41.8.1.3", {"start": v(116.97, 71.5) * mm, "end": v(116.97, 90.55) * mm});
            skLineSegment(sketch, "E41.8.2.0", {"start": v(116.97, 44.58) * mm, "end": v(97.92, 44.58) * mm});
            skLineSegment(sketch, "E41.8.2.1", {"start": v(97.92, 44.58) * mm, "end": v(97.92, 63.63) * mm});
            skLineSegment(sketch, "E41.8.2.2", {"start": v(116.97, 63.63) * mm, "end": v(97.92, 63.63) * mm});
            skLineSegment(sketch, "E41.8.2.3", {"start": v(116.97, 44.58) * mm, "end": v(116.97, 63.63) * mm});
            skLineSegment(sketch, "E41.8.3.0", {"start": v(116.97, 17.65) * mm, "end": v(97.92, 17.65) * mm});
            skLineSegment(sketch, "E41.8.3.1", {"start": v(97.92, 17.65) * mm, "end": v(97.92, 36.7) * mm});
            skLineSegment(sketch, "E41.8.3.2", {"start": v(116.97, 36.7) * mm, "end": v(97.92, 36.7) * mm});
            skLineSegment(sketch, "E41.8.3.3", {"start": v(116.97, 17.65) * mm, "end": v(116.97, 36.7) * mm});
            skLineSegment(sketch, "E41.8.4.0", {"start": v(116.97, -9.27) * mm, "end": v(97.92, -9.27) * mm});
            skLineSegment(sketch, "E41.8.4.1", {"start": v(97.92, -9.27) * mm, "end": v(97.92, 9.78) * mm});
            skLineSegment(sketch, "E41.8.4.2", {"start": v(116.97, 9.78) * mm, "end": v(97.92, 9.78) * mm});
            skLineSegment(sketch, "E41.8.4.3", {"start": v(116.97, -9.27) * mm, "end": v(116.97, 9.78) * mm});
            skLineSegment(sketch, "E41.8.5.0", {"start": v(116.97, -36.2) * mm, "end": v(97.92, -36.2) * mm});
            skLineSegment(sketch, "E41.8.5.1", {"start": v(97.92, -36.2) * mm, "end": v(97.92, -17.15) * mm});
            skLineSegment(sketch, "E41.8.5.2", {"start": v(116.97, -17.15) * mm, "end": v(97.92, -17.15) * mm});
            skLineSegment(sketch, "E41.8.5.3", {"start": v(116.97, -36.2) * mm, "end": v(116.97, -17.15) * mm});
            skLineSegment(sketch, "E41.8.6.0", {"start": v(116.97, -63.12) * mm, "end": v(97.92, -63.12) * mm});
            skLineSegment(sketch, "E41.8.6.1", {"start": v(97.92, -63.12) * mm, "end": v(97.92, -44.07) * mm});
            skLineSegment(sketch, "E41.8.6.2", {"start": v(116.97, -44.07) * mm, "end": v(97.92, -44.07) * mm});
            skLineSegment(sketch, "E41.8.6.3", {"start": v(116.97, -63.12) * mm, "end": v(116.97, -44.07) * mm});
            skLineSegment(sketch, "E41.8.7.0", {"start": v(116.97, -90.04) * mm, "end": v(97.92, -90.04) * mm});
            skLineSegment(sketch, "E41.8.7.1", {"start": v(97.92, -90.04) * mm, "end": v(97.92, -71) * mm});
            skLineSegment(sketch, "E41.8.7.2", {"start": v(116.97, -71) * mm, "end": v(97.92, -71) * mm});
            skLineSegment(sketch, "E41.8.7.3", {"start": v(116.97, -90.04) * mm, "end": v(116.97, -71) * mm});
            skLineSegment(sketch, "E41.8.8.0", {"start": v(116.97, -116.97) * mm, "end": v(97.92, -116.97) * mm});
            skLineSegment(sketch, "E41.8.8.1", {"start": v(97.92, -116.97) * mm, "end": v(97.92, -97.92) * mm});
            skLineSegment(sketch, "E41.8.8.2", {"start": v(116.97, -97.92) * mm, "end": v(97.92, -97.92) * mm});
            skLineSegment(sketch, "E41.8.8.3", {"start": v(116.97, -116.97) * mm, "end": v(116.97, -97.92) * mm});
            skLineSegment(sketch, "E41.direction1", {"start": v(-117.47, 98.42) * mm, "end": v(-90.55, 98.42) * mm, "construction": true});
            skLineSegment(sketch, "E41.direction2", {"start": v(-117.47, 98.42) * mm, "end": v(-117.47, 71.5) * mm, "construction": true});
            skSolve(sketch);
        }
        {
            var Q0;
            Q0 = qSketchRegion(id + "F16", true);
            extrude(context, id + "F17", {"entities" : qUnion([Q0]), "operationType" : NewBodyOperationType.REMOVE, "endBound" : BoundingType.THROUGH_ALL, "oppositeDirection" : true, "depth" : 25.4 * mm});
        }
    });
